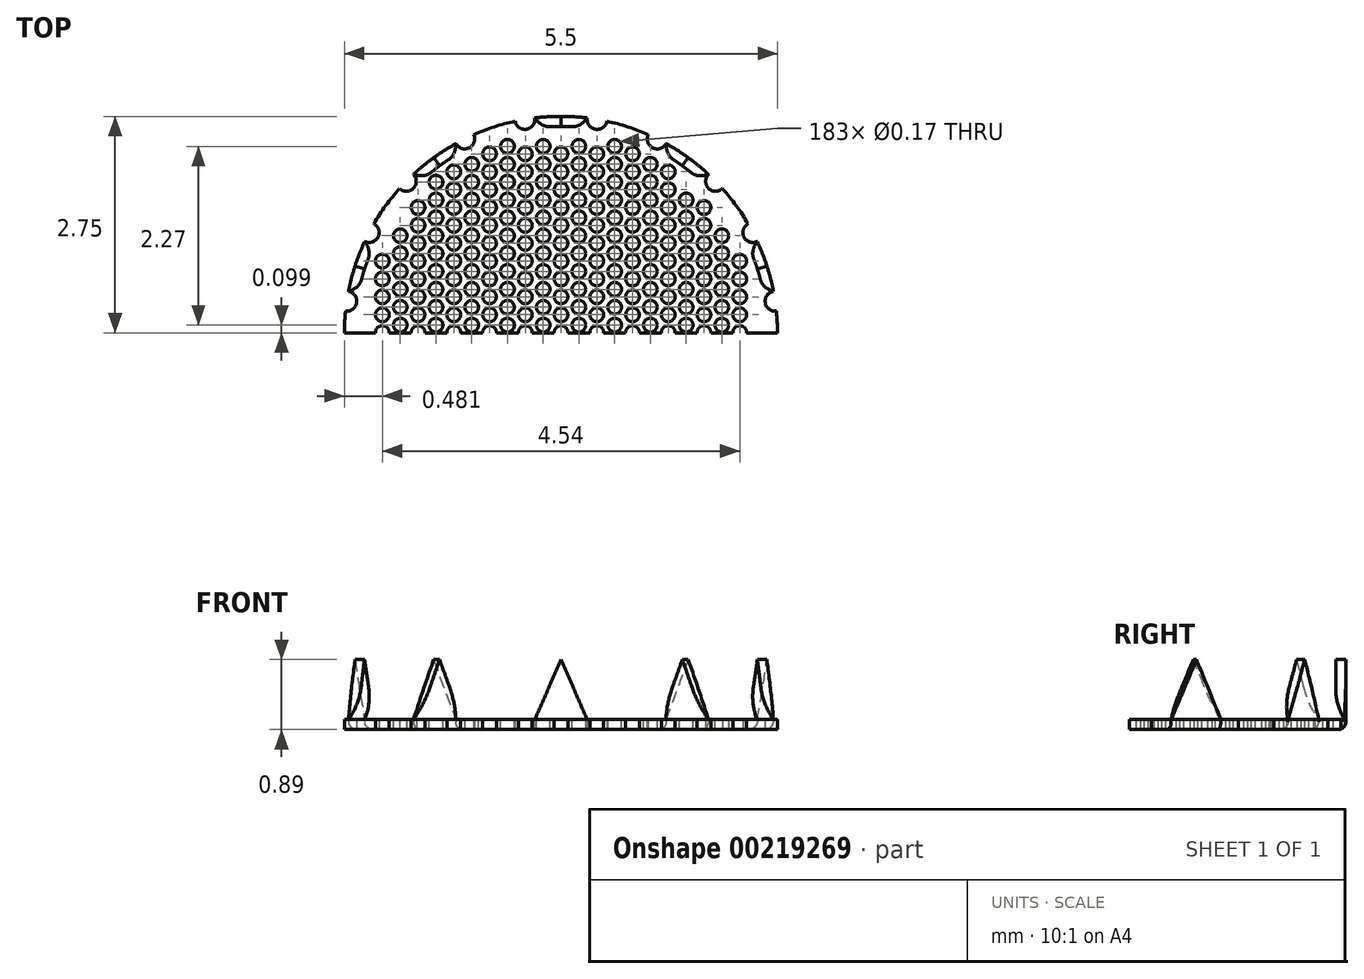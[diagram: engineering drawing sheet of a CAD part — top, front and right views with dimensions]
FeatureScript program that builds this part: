
annotation { "Feature Type Name" : "Feature", "Feature Type Description" : "" }
export const myFeature = defineFeature(function(context is Context, id is Id, definition is map)
    precondition{}
    {
        {
            var Q0;
            Q0=qCreatedBy(makeId("Top.planeOp"),FACE);
            var sketch = newSketch(context, id + "F0", { "sketchPlane" : qUnion([Q0])});
            skCircle(sketch, "E0", {"center": v(0, 0) * mm, "radius": 2.5 * mm});
            skArc(sketch, "E1", {"start": v(0.33, 2.73) * mm, "mid": v(0, 2.75) * mm, "end": v(-0.33, 2.73) * mm});
            skPoint(sketch, "E2", {"position": v(0, 2.75) * mm});
            skLineSegment(sketch, "E3", {"start": v(-3.94, 3.51) * mm, "end": v(3.7, 3.51) * mm, "construction": true});
            skLineSegment(sketch, "E4", {"start": v(0, 3.51) * mm, "end": v(-0.33, 2.73) * mm});
            skLineSegment(sketch, "E5", {"start": v(0, 3.51) * mm, "end": v(0.33, 2.73) * mm});
            skLineSegment(sketch, "E6.1.0", {"start": v(-2.06, 2.84) * mm, "end": v(-1.87, 2.01) * mm});
            skLineSegment(sketch, "E6.1.1", {"start": v(-2.06, 2.84) * mm, "end": v(-1.34, 2.4) * mm});
            skLineSegment(sketch, "E6.2.0", {"start": v(-3.34, 1.09) * mm, "end": v(-2.7, 0.53) * mm});
            skLineSegment(sketch, "E6.2.1", {"start": v(-3.34, 1.09) * mm, "end": v(-2.5, 1.16) * mm});
            skLineSegment(sketch, "E6.3.0", {"start": v(-3.34, -1.09) * mm, "end": v(-2.5, -1.16) * mm});
            skLineSegment(sketch, "E6.3.1", {"start": v(-3.34, -1.09) * mm, "end": v(-2.7, -0.53) * mm});
            skLineSegment(sketch, "E6.4.0", {"start": v(-2.06, -2.84) * mm, "end": v(-1.34, -2.4) * mm});
            skLineSegment(sketch, "E6.4.1", {"start": v(-2.06, -2.84) * mm, "end": v(-1.87, -2.01) * mm});
            skLineSegment(sketch, "E6.5.0", {"start": v(0, -3.51) * mm, "end": v(0.33, -2.73) * mm});
            skLineSegment(sketch, "E6.5.1", {"start": v(0, -3.51) * mm, "end": v(-0.33, -2.73) * mm});
            skLineSegment(sketch, "E6.6.0", {"start": v(2.06, -2.84) * mm, "end": v(1.87, -2.01) * mm});
            skLineSegment(sketch, "E6.6.1", {"start": v(2.06, -2.84) * mm, "end": v(1.34, -2.4) * mm});
            skLineSegment(sketch, "E6.7.0", {"start": v(3.34, -1.09) * mm, "end": v(2.7, -0.53) * mm});
            skLineSegment(sketch, "E6.7.1", {"start": v(3.34, -1.09) * mm, "end": v(2.5, -1.16) * mm});
            skLineSegment(sketch, "E6.8.0", {"start": v(3.34, 1.09) * mm, "end": v(2.5, 1.16) * mm});
            skLineSegment(sketch, "E6.8.1", {"start": v(3.34, 1.09) * mm, "end": v(2.7, 0.53) * mm});
            skLineSegment(sketch, "E6.9.0", {"start": v(2.06, 2.84) * mm, "end": v(1.34, 2.4) * mm});
            skLineSegment(sketch, "E6.9.1", {"start": v(2.06, 2.84) * mm, "end": v(1.87, 2.01) * mm});
            skCircle(sketch, "E7", {"center": v(0, 0) * mm, "radius": 2.62 * mm});
            skPoint(sketch, "E8", {"position": v(0.46, 2.71) * mm});
            skArc(sketch, "E9", {"start": v(0.33, 2.73) * mm, "mid": v(0.44, 2.59) * mm, "end": v(0.58, 2.69) * mm});
            skArc(sketch, "E10.1.0", {"start": v(-1.34, 2.4) * mm, "mid": v(-1.17, 2.35) * mm, "end": v(-1.1, 2.52) * mm});
            skArc(sketch, "E10.2.0", {"start": v(-2.5, 1.16) * mm, "mid": v(-2.32, 1.21) * mm, "end": v(-2.38, 1.38) * mm});
            skArc(sketch, "E10.3.0", {"start": v(-2.7, -0.53) * mm, "mid": v(-2.6, -0.38) * mm, "end": v(-2.74, -0.28) * mm});
            skArc(sketch, "E10.4.0", {"start": v(-1.87, -2.01) * mm, "mid": v(-1.87, -1.84) * mm, "end": v(-2.05, -1.83) * mm});
            skArc(sketch, "E10.5.0", {"start": v(-0.33, -2.73) * mm, "mid": v(-0.44, -2.59) * mm, "end": v(-0.58, -2.69) * mm});
            skArc(sketch, "E10.6.0", {"start": v(1.34, -2.4) * mm, "mid": v(1.17, -2.35) * mm, "end": v(1.1, -2.52) * mm});
            skArc(sketch, "E10.7.0", {"start": v(2.5, -1.16) * mm, "mid": v(2.32, -1.21) * mm, "end": v(2.38, -1.38) * mm});
            skArc(sketch, "E10.8.0", {"start": v(2.7, 0.53) * mm, "mid": v(2.6, 0.38) * mm, "end": v(2.74, 0.28) * mm});
            skArc(sketch, "E10.9.0", {"start": v(1.87, 2.01) * mm, "mid": v(1.87, 1.84) * mm, "end": v(2.05, 1.83) * mm});
            skArc(sketch, "E11", {"start": v(-0.58, 2.69) * mm, "mid": v(-0.44, 2.59) * mm, "end": v(-0.33, 2.73) * mm});
            skArc(sketch, "E12.trimOffspring", {"start": v(-0.58, 2.69) * mm, "mid": v(-0.85, 2.62) * mm, "end": v(-1.1, 2.52) * mm});
            skArc(sketch, "E13.1.0", {"start": v(-2.05, 1.83) * mm, "mid": v(-1.87, 1.84) * mm, "end": v(-1.87, 2.01) * mm});
            skArc(sketch, "E13.2.0", {"start": v(-2.74, 0.28) * mm, "mid": v(-2.6, 0.38) * mm, "end": v(-2.7, 0.53) * mm});
            skArc(sketch, "E13.3.0", {"start": v(-2.38, -1.38) * mm, "mid": v(-2.32, -1.21) * mm, "end": v(-2.5, -1.16) * mm});
            skArc(sketch, "E13.4.0", {"start": v(-1.1, -2.52) * mm, "mid": v(-1.17, -2.35) * mm, "end": v(-1.34, -2.4) * mm});
            skArc(sketch, "E13.5.0", {"start": v(0.58, -2.69) * mm, "mid": v(0.44, -2.59) * mm, "end": v(0.33, -2.73) * mm});
            skArc(sketch, "E13.6.0", {"start": v(2.05, -1.83) * mm, "mid": v(1.87, -1.84) * mm, "end": v(1.87, -2.01) * mm});
            skArc(sketch, "E13.7.0", {"start": v(2.74, -0.28) * mm, "mid": v(2.6, -0.38) * mm, "end": v(2.7, -0.53) * mm});
            skArc(sketch, "E13.8.0", {"start": v(2.38, 1.38) * mm, "mid": v(2.32, 1.21) * mm, "end": v(2.5, 1.16) * mm});
            skArc(sketch, "E13.9.0", {"start": v(1.1, 2.52) * mm, "mid": v(1.17, 2.35) * mm, "end": v(1.34, 2.4) * mm});
            skArc(sketch, "E14.trimOffspring", {"start": v(1.1, 2.52) * mm, "mid": v(0.85, 2.62) * mm, "end": v(0.58, 2.69) * mm});
            skArc(sketch, "E15.trimOffspring", {"start": v(1.87, 2.01) * mm, "mid": v(1.62, 2.22) * mm, "end": v(1.34, 2.4) * mm});
            skArc(sketch, "E16.trimOffspring", {"start": v(2.38, 1.38) * mm, "mid": v(2.22, 1.62) * mm, "end": v(2.05, 1.83) * mm});
            skArc(sketch, "E17.trimOffspring", {"start": v(2.7, 0.53) * mm, "mid": v(2.62, 0.85) * mm, "end": v(2.5, 1.16) * mm});
            skArc(sketch, "E18.trimOffspring", {"start": v(2.74, -0.28) * mm, "mid": v(2.75, 0) * mm, "end": v(2.74, 0.28) * mm});
            skArc(sketch, "E19.trimOffspring", {"start": v(2.5, -1.16) * mm, "mid": v(2.62, -0.85) * mm, "end": v(2.7, -0.53) * mm});
            skArc(sketch, "E20.trimOffspring", {"start": v(2.05, -1.83) * mm, "mid": v(2.22, -1.62) * mm, "end": v(2.38, -1.38) * mm});
            skArc(sketch, "E21.trimOffspring", {"start": v(1.34, -2.4) * mm, "mid": v(1.62, -2.22) * mm, "end": v(1.87, -2.01) * mm});
            skArc(sketch, "E22.trimOffspring", {"start": v(-2.38, -1.38) * mm, "mid": v(-2.22, -1.62) * mm, "end": v(-2.05, -1.83) * mm});
            skArc(sketch, "E23.trimOffspring", {"start": v(-1.87, -2.01) * mm, "mid": v(-1.62, -2.22) * mm, "end": v(-1.34, -2.4) * mm});
            skArc(sketch, "E24.trimOffspring", {"start": v(-1.1, -2.52) * mm, "mid": v(-0.85, -2.62) * mm, "end": v(-0.58, -2.69) * mm});
            skArc(sketch, "E25.trimOffspring", {"start": v(-0.33, -2.73) * mm, "mid": v(0, -2.75) * mm, "end": v(0.33, -2.73) * mm});
            skArc(sketch, "E26.trimOffspring", {"start": v(0.58, -2.69) * mm, "mid": v(0.85, -2.62) * mm, "end": v(1.1, -2.52) * mm});
            skArc(sketch, "E27.trimOffspring", {"start": v(-2.7, -0.53) * mm, "mid": v(-2.62, -0.85) * mm, "end": v(-2.5, -1.16) * mm});
            skArc(sketch, "E28.trimOffspring", {"start": v(-2.74, 0.28) * mm, "mid": v(-2.75, 0) * mm, "end": v(-2.74, -0.28) * mm});
            skArc(sketch, "E29.trimOffspring", {"start": v(-2.5, 1.16) * mm, "mid": v(-2.62, 0.85) * mm, "end": v(-2.7, 0.53) * mm});
            skArc(sketch, "E30.trimOffspring", {"start": v(-2.05, 1.83) * mm, "mid": v(-2.22, 1.62) * mm, "end": v(-2.38, 1.38) * mm});
            skArc(sketch, "E31.trimOffspring", {"start": v(-1.34, 2.4) * mm, "mid": v(-1.62, 2.22) * mm, "end": v(-1.87, 2.01) * mm});
            skSolve(sketch);
        }
        {
            var Q0;
            Q0=qSketchRegion(id+"F0",true);
            var Q1;
            Q1=makeQuery(id+"F0.imprint","IMPRINT",FACE,{"disambiguationData":[TD([[makeQuery(id+"F0.imprint","IMPRINT",EDGE,{"derivedFrom":sQuery(id+"F0.wireOp",EDGE,"E0")}),1.0]])]});
            extrude(context, id + "F1", {"entities" : qUnion([Q0, Q1]), "depth" : 0.13 * mm});
        }
        {
            var Q0;
            Q0=makeQuery(id+"F1.opExtrude","CAP_FACE",FACE,{"disambiguationData":[OSD([sQuery(id+"F0.wireOp",EDGE,"E1"),sQuery(id+"F0.wireOp",EDGE,"E4"),sQuery(id+"F0.wireOp",EDGE,"E5"),sQuery(id+"F0.wireOp",EDGE,"E6.1.0"),sQuery(id+"F0.wireOp",EDGE,"E6.1.1"),sQuery(id+"F0.wireOp",EDGE,"E6.2.0"),sQuery(id+"F0.wireOp",EDGE,"E6.2.1"),sQuery(id+"F0.wireOp",EDGE,"E6.3.0"),sQuery(id+"F0.wireOp",EDGE,"E6.3.1"),sQuery(id+"F0.wireOp",EDGE,"E6.4.0"),sQuery(id+"F0.wireOp",EDGE,"E6.4.1"),sQuery(id+"F0.wireOp",EDGE,"E6.5.0"),sQuery(id+"F0.wireOp",EDGE,"E6.5.1"),sQuery(id+"F0.wireOp",EDGE,"E6.6.0"),sQuery(id+"F0.wireOp",EDGE,"E6.6.1"),sQuery(id+"F0.wireOp",EDGE,"E6.7.0"),sQuery(id+"F0.wireOp",EDGE,"E6.7.1"),sQuery(id+"F0.wireOp",EDGE,"E6.8.0"),sQuery(id+"F0.wireOp",EDGE,"E6.8.1"),sQuery(id+"F0.wireOp",EDGE,"E6.9.0"),sQuery(id+"F0.wireOp",EDGE,"E6.9.1")])],"isStart":false});
            cPlane(context, id + "F2", {"entities" : qUnion([Q0]), "cplaneType" : CPlaneType.OFFSET, "offset" : 0 * mm, "width" : 150 * mm, "height" : 150 * mm});
        }
        {
            var Q0;
            Q0=qCreatedBy(id+"F2.planeOp",FACE);
            var sketch = newSketch(context, id + "F3", { "sketchPlane" : qUnion([Q0])});
            skCircle(sketch, "E32.2.1.8", {"center": v(-2.04, 1.23) * mm, "radius": 0.09 * mm});
            skCircle(sketch, "E32.2.1.9", {"center": v(-2.04, 1) * mm, "radius": 0.09 * mm});
            skCircle(sketch, "E32.0.1.10", {"center": v(-2.27, 0.91) * mm, "radius": 0.09 * mm});
            skCircle(sketch, "E32.2.1.10", {"center": v(-2.04, 0.78) * mm, "radius": 0.09 * mm});
            skCircle(sketch, "E32.2.2.5", {"center": v(-1.59, 1.91) * mm, "radius": 0.09 * mm});
            skCircle(sketch, "E32.2.2.6", {"center": v(-1.59, 1.69) * mm, "radius": 0.09 * mm});
            skCircle(sketch, "E32.0.2.7", {"center": v(-1.82, 1.6) * mm, "radius": 0.09 * mm});
            skCircle(sketch, "E32.2.2.7", {"center": v(-1.59, 1.46) * mm, "radius": 0.09 * mm});
            skCircle(sketch, "E32.0.2.8", {"center": v(-1.82, 1.36) * mm, "radius": 0.09 * mm});
            skCircle(sketch, "E32.2.2.8", {"center": v(-1.59, 1.23) * mm, "radius": 0.09 * mm});
            skCircle(sketch, "E32.0.2.9", {"center": v(-1.82, 1.14) * mm, "radius": 0.09 * mm});
            skCircle(sketch, "E32.2.2.9", {"center": v(-1.59, 1) * mm, "radius": 0.09 * mm});
            skCircle(sketch, "E32.0.2.10", {"center": v(-1.82, 0.91) * mm, "radius": 0.09 * mm});
            skCircle(sketch, "E32.2.2.10", {"center": v(-1.59, 0.78) * mm, "radius": 0.09 * mm});
            skCircle(sketch, "E32.2.3.4", {"center": v(-1.13, 2.14) * mm, "radius": 0.09 * mm});
            skCircle(sketch, "E32.0.3.5", {"center": v(-1.36, 2.05) * mm, "radius": 0.09 * mm});
            skCircle(sketch, "E32.2.3.5", {"center": v(-1.13, 1.91) * mm, "radius": 0.09 * mm});
            skCircle(sketch, "E32.0.3.6", {"center": v(-1.36, 1.82) * mm, "radius": 0.09 * mm});
            skCircle(sketch, "E32.2.3.6", {"center": v(-1.13, 1.69) * mm, "radius": 0.09 * mm});
            skCircle(sketch, "E32.0.3.7", {"center": v(-1.36, 1.6) * mm, "radius": 0.09 * mm});
            skCircle(sketch, "E32.2.3.7", {"center": v(-1.13, 1.46) * mm, "radius": 0.09 * mm});
            skCircle(sketch, "E32.0.3.8", {"center": v(-1.36, 1.36) * mm, "radius": 0.09 * mm});
            skCircle(sketch, "E32.2.3.8", {"center": v(-1.13, 1.23) * mm, "radius": 0.09 * mm});
            skCircle(sketch, "E32.0.3.9", {"center": v(-1.36, 1.14) * mm, "radius": 0.09 * mm});
            skCircle(sketch, "E32.2.3.9", {"center": v(-1.13, 1) * mm, "radius": 0.09 * mm});
            skCircle(sketch, "E32.0.3.10", {"center": v(-1.36, 0.91) * mm, "radius": 0.09 * mm});
            skCircle(sketch, "E32.2.3.10", {"center": v(-1.13, 0.78) * mm, "radius": 0.09 * mm});
            skCircle(sketch, "E32.2.4.3", {"center": v(-0.68, 2.37) * mm, "radius": 0.09 * mm});
            skCircle(sketch, "E32.0.4.4", {"center": v(-0.9, 2.27) * mm, "radius": 0.09 * mm});
            skCircle(sketch, "E32.2.4.4", {"center": v(-0.68, 2.14) * mm, "radius": 0.09 * mm});
            skCircle(sketch, "E32.0.4.5", {"center": v(-0.9, 2.05) * mm, "radius": 0.09 * mm});
            skCircle(sketch, "E32.2.4.5", {"center": v(-0.68, 1.91) * mm, "radius": 0.09 * mm});
            skCircle(sketch, "E32.0.4.6", {"center": v(-0.9, 1.82) * mm, "radius": 0.09 * mm});
            skCircle(sketch, "E32.2.4.6", {"center": v(-0.68, 1.69) * mm, "radius": 0.09 * mm});
            skCircle(sketch, "E32.0.4.7", {"center": v(-0.9, 1.6) * mm, "radius": 0.09 * mm});
            skCircle(sketch, "E32.2.4.7", {"center": v(-0.68, 1.46) * mm, "radius": 0.09 * mm});
            skCircle(sketch, "E32.0.4.8", {"center": v(-0.9, 1.36) * mm, "radius": 0.09 * mm});
            skCircle(sketch, "E32.2.4.8", {"center": v(-0.68, 1.23) * mm, "radius": 0.09 * mm});
            skCircle(sketch, "E32.0.4.9", {"center": v(-0.9, 1.14) * mm, "radius": 0.09 * mm});
            skCircle(sketch, "E32.2.4.9", {"center": v(-0.68, 1) * mm, "radius": 0.09 * mm});
            skCircle(sketch, "E32.0.4.10", {"center": v(-0.9, 0.91) * mm, "radius": 0.09 * mm});
            skCircle(sketch, "E32.2.4.10", {"center": v(-0.68, 0.78) * mm, "radius": 0.09 * mm});
            skCircle(sketch, "E32.2.5.3", {"center": v(-0.23, 2.37) * mm, "radius": 0.09 * mm});
            skCircle(sketch, "E32.0.5.4", {"center": v(-0.45, 2.27) * mm, "radius": 0.09 * mm});
            skCircle(sketch, "E32.2.5.4", {"center": v(-0.23, 2.14) * mm, "radius": 0.09 * mm});
            skCircle(sketch, "E32.0.5.5", {"center": v(-0.45, 2.05) * mm, "radius": 0.09 * mm});
            skCircle(sketch, "E32.2.5.5", {"center": v(-0.23, 1.91) * mm, "radius": 0.09 * mm});
            skCircle(sketch, "E32.0.5.6", {"center": v(-0.45, 1.82) * mm, "radius": 0.09 * mm});
            skCircle(sketch, "E32.2.5.6", {"center": v(-0.23, 1.69) * mm, "radius": 0.09 * mm});
            skCircle(sketch, "E32.0.5.7", {"center": v(-0.45, 1.6) * mm, "radius": 0.09 * mm});
            skCircle(sketch, "E32.2.5.7", {"center": v(-0.23, 1.46) * mm, "radius": 0.09 * mm});
            skCircle(sketch, "E32.0.5.8", {"center": v(-0.45, 1.36) * mm, "radius": 0.09 * mm});
            skCircle(sketch, "E32.2.5.8", {"center": v(-0.23, 1.23) * mm, "radius": 0.09 * mm});
            skCircle(sketch, "E32.0.5.9", {"center": v(-0.45, 1.14) * mm, "radius": 0.09 * mm});
            skCircle(sketch, "E32.2.5.9", {"center": v(-0.23, 1) * mm, "radius": 0.09 * mm});
            skCircle(sketch, "E32.0.5.10", {"center": v(-0.45, 0.91) * mm, "radius": 0.09 * mm});
            skCircle(sketch, "E32.2.5.10", {"center": v(-0.23, 0.78) * mm, "radius": 0.09 * mm});
            skCircle(sketch, "E32.2.6.3", {"center": v(0.23, 2.37) * mm, "radius": 0.09 * mm});
            skCircle(sketch, "E32.0.6.4", {"center": v(0, 2.27) * mm, "radius": 0.09 * mm});
            skCircle(sketch, "E32.2.6.4", {"center": v(0.23, 2.14) * mm, "radius": 0.09 * mm});
            skCircle(sketch, "E32.0.6.5", {"center": v(0, 2.05) * mm, "radius": 0.09 * mm});
            skCircle(sketch, "E32.2.6.5", {"center": v(0.23, 1.91) * mm, "radius": 0.09 * mm});
            skCircle(sketch, "E32.0.6.6", {"center": v(0, 1.82) * mm, "radius": 0.09 * mm});
            skCircle(sketch, "E32.2.6.6", {"center": v(0.23, 1.69) * mm, "radius": 0.09 * mm});
            skCircle(sketch, "E32.0.6.7", {"center": v(0, 1.6) * mm, "radius": 0.09 * mm});
            skCircle(sketch, "E32.2.6.7", {"center": v(0.23, 1.46) * mm, "radius": 0.09 * mm});
            skCircle(sketch, "E32.0.6.8", {"center": v(0, 1.36) * mm, "radius": 0.09 * mm});
            skCircle(sketch, "E32.2.6.8", {"center": v(0.23, 1.23) * mm, "radius": 0.09 * mm});
            skCircle(sketch, "E32.0.6.9", {"center": v(0, 1.14) * mm, "radius": 0.09 * mm});
            skCircle(sketch, "E32.2.6.9", {"center": v(0.23, 1) * mm, "radius": 0.09 * mm});
            skCircle(sketch, "E32.0.6.10", {"center": v(0, 0.91) * mm, "radius": 0.09 * mm});
            skCircle(sketch, "E32.2.6.10", {"center": v(0.23, 0.78) * mm, "radius": 0.09 * mm});
            skCircle(sketch, "E32.2.7.3", {"center": v(0.68, 2.37) * mm, "radius": 0.09 * mm});
            skCircle(sketch, "E32.0.7.4", {"center": v(0.45, 2.27) * mm, "radius": 0.09 * mm});
            skCircle(sketch, "E32.2.7.4", {"center": v(0.68, 2.14) * mm, "radius": 0.09 * mm});
            skCircle(sketch, "E32.0.7.5", {"center": v(0.45, 2.05) * mm, "radius": 0.09 * mm});
            skCircle(sketch, "E32.2.7.5", {"center": v(0.68, 1.91) * mm, "radius": 0.09 * mm});
            skCircle(sketch, "E32.0.7.6", {"center": v(0.45, 1.82) * mm, "radius": 0.09 * mm});
            skCircle(sketch, "E32.2.7.6", {"center": v(0.68, 1.69) * mm, "radius": 0.09 * mm});
            skCircle(sketch, "E32.0.7.7", {"center": v(0.45, 1.6) * mm, "radius": 0.09 * mm});
            skCircle(sketch, "E32.2.7.7", {"center": v(0.68, 1.46) * mm, "radius": 0.09 * mm});
            skCircle(sketch, "E32.0.7.8", {"center": v(0.45, 1.36) * mm, "radius": 0.09 * mm});
            skCircle(sketch, "E32.2.7.8", {"center": v(0.68, 1.23) * mm, "radius": 0.09 * mm});
            skCircle(sketch, "E32.0.7.9", {"center": v(0.45, 1.14) * mm, "radius": 0.09 * mm});
            skCircle(sketch, "E32.2.7.9", {"center": v(0.68, 1) * mm, "radius": 0.09 * mm});
            skCircle(sketch, "E32.0.7.10", {"center": v(0.45, 0.91) * mm, "radius": 0.09 * mm});
            skCircle(sketch, "E32.2.7.10", {"center": v(0.68, 0.78) * mm, "radius": 0.09 * mm});
            skCircle(sketch, "E32.0.8.4", {"center": v(0.9, 2.27) * mm, "radius": 0.09 * mm});
            skCircle(sketch, "E32.2.8.4", {"center": v(1.14, 2.14) * mm, "radius": 0.09 * mm});
            skCircle(sketch, "E32.0.8.5", {"center": v(0.9, 2.05) * mm, "radius": 0.09 * mm});
            skCircle(sketch, "E32.2.8.5", {"center": v(1.14, 1.91) * mm, "radius": 0.09 * mm});
            skCircle(sketch, "E32.0.8.6", {"center": v(0.9, 1.82) * mm, "radius": 0.09 * mm});
            skCircle(sketch, "E32.2.8.6", {"center": v(1.14, 1.69) * mm, "radius": 0.09 * mm});
            skCircle(sketch, "E32.0.8.7", {"center": v(0.9, 1.6) * mm, "radius": 0.09 * mm});
            skCircle(sketch, "E32.2.8.7", {"center": v(1.14, 1.46) * mm, "radius": 0.09 * mm});
            skCircle(sketch, "E32.0.8.8", {"center": v(0.9, 1.36) * mm, "radius": 0.09 * mm});
            skCircle(sketch, "E32.2.8.8", {"center": v(1.14, 1.23) * mm, "radius": 0.09 * mm});
            skCircle(sketch, "E32.0.8.9", {"center": v(0.9, 1.14) * mm, "radius": 0.09 * mm});
            skCircle(sketch, "E32.2.8.9", {"center": v(1.14, 1) * mm, "radius": 0.09 * mm});
            skCircle(sketch, "E32.0.8.10", {"center": v(0.9, 0.91) * mm, "radius": 0.09 * mm});
            skCircle(sketch, "E32.2.8.10", {"center": v(1.14, 0.78) * mm, "radius": 0.09 * mm});
            skCircle(sketch, "E32.0.9.5", {"center": v(1.36, 2.05) * mm, "radius": 0.09 * mm});
            skCircle(sketch, "E32.0.9.6", {"center": v(1.36, 1.82) * mm, "radius": 0.09 * mm});
            skCircle(sketch, "E32.2.9.6", {"center": v(1.6, 1.69) * mm, "radius": 0.09 * mm});
            skCircle(sketch, "E32.0.9.7", {"center": v(1.36, 1.6) * mm, "radius": 0.09 * mm});
            skCircle(sketch, "E32.2.9.7", {"center": v(1.6, 1.46) * mm, "radius": 0.09 * mm});
            skCircle(sketch, "E32.0.9.8", {"center": v(1.36, 1.36) * mm, "radius": 0.09 * mm});
            skCircle(sketch, "E32.2.9.8", {"center": v(1.6, 1.23) * mm, "radius": 0.09 * mm});
            skCircle(sketch, "E32.0.9.9", {"center": v(1.36, 1.14) * mm, "radius": 0.09 * mm});
            skCircle(sketch, "E32.2.9.9", {"center": v(1.6, 1) * mm, "radius": 0.09 * mm});
            skCircle(sketch, "E32.0.9.10", {"center": v(1.36, 0.91) * mm, "radius": 0.09 * mm});
            skCircle(sketch, "E32.2.9.10", {"center": v(1.6, 0.78) * mm, "radius": 0.09 * mm});
            skCircle(sketch, "E32.0.10.7", {"center": v(1.82, 1.6) * mm, "radius": 0.09 * mm});
            skCircle(sketch, "E32.0.10.8", {"center": v(1.82, 1.36) * mm, "radius": 0.09 * mm});
            skCircle(sketch, "E32.2.10.8", {"center": v(2.04, 1.23) * mm, "radius": 0.09 * mm});
            skCircle(sketch, "E32.0.10.9", {"center": v(1.82, 1.14) * mm, "radius": 0.09 * mm});
            skCircle(sketch, "E32.2.10.9", {"center": v(2.04, 1) * mm, "radius": 0.09 * mm});
            skCircle(sketch, "E32.0.10.10", {"center": v(1.82, 0.91) * mm, "radius": 0.09 * mm});
            skCircle(sketch, "E32.2.10.10", {"center": v(2.04, 0.78) * mm, "radius": 0.09 * mm});
            skCircle(sketch, "E33.0.1.11", {"center": v(-2.27, 0.68) * mm, "radius": 0.09 * mm});
            skCircle(sketch, "E33.2.1.11", {"center": v(-2.04, 0.55) * mm, "radius": 0.09 * mm});
            skCircle(sketch, "E33.0.1.12", {"center": v(-2.27, 0.46) * mm, "radius": 0.09 * mm});
            skCircle(sketch, "E33.2.1.12", {"center": v(-2.04, 0.33) * mm, "radius": 0.09 * mm});
            skCircle(sketch, "E33.0.1.13", {"center": v(-2.27, 0.23) * mm, "radius": 0.09 * mm});
            skCircle(sketch, "E33.2.1.13", {"center": v(-2.04, 0.1) * mm, "radius": 0.09 * mm});
            skCircle(sketch, "E33.0.1.14", {"center": v(-2.27, 0) * mm, "radius": 0.09 * mm});
            skCircle(sketch, "E33.2.1.14", {"center": v(-2.04, -0.13) * mm, "radius": 0.09 * mm});
            skCircle(sketch, "E33.0.1.15", {"center": v(-2.27, -0.22) * mm, "radius": 0.09 * mm});
            skCircle(sketch, "E33.2.1.15", {"center": v(-2.04, -0.36) * mm, "radius": 0.09 * mm});
            skCircle(sketch, "E33.0.1.16", {"center": v(-2.27, -0.45) * mm, "radius": 0.09 * mm});
            skCircle(sketch, "E33.2.1.16", {"center": v(-2.04, -0.58) * mm, "radius": 0.09 * mm});
            skCircle(sketch, "E33.0.1.17", {"center": v(-2.27, -0.68) * mm, "radius": 0.09 * mm});
            skCircle(sketch, "E33.2.1.17", {"center": v(-2.04, -0.8) * mm, "radius": 0.09 * mm});
            skCircle(sketch, "E33.0.1.18", {"center": v(-2.27, -0.9) * mm, "radius": 0.09 * mm});
            skCircle(sketch, "E33.2.1.18", {"center": v(-2.04, -1.04) * mm, "radius": 0.09 * mm});
            skCircle(sketch, "E33.2.1.19", {"center": v(-2.04, -1.26) * mm, "radius": 0.09 * mm});
            skCircle(sketch, "E33.0.2.11", {"center": v(-1.82, 0.68) * mm, "radius": 0.09 * mm});
            skCircle(sketch, "E33.2.2.11", {"center": v(-1.59, 0.55) * mm, "radius": 0.09 * mm});
            skCircle(sketch, "E33.0.2.12", {"center": v(-1.82, 0.46) * mm, "radius": 0.09 * mm});
            skCircle(sketch, "E33.2.2.12", {"center": v(-1.59, 0.33) * mm, "radius": 0.09 * mm});
            skCircle(sketch, "E33.0.2.13", {"center": v(-1.82, 0.23) * mm, "radius": 0.09 * mm});
            skCircle(sketch, "E33.2.2.13", {"center": v(-1.59, 0.1) * mm, "radius": 0.09 * mm});
            skCircle(sketch, "E33.0.2.14", {"center": v(-1.82, 0) * mm, "radius": 0.09 * mm});
            skCircle(sketch, "E33.2.2.14", {"center": v(-1.59, -0.13) * mm, "radius": 0.09 * mm});
            skCircle(sketch, "E33.0.2.15", {"center": v(-1.82, -0.22) * mm, "radius": 0.09 * mm});
            skCircle(sketch, "E33.2.2.15", {"center": v(-1.59, -0.36) * mm, "radius": 0.09 * mm});
            skCircle(sketch, "E33.0.2.16", {"center": v(-1.82, -0.45) * mm, "radius": 0.09 * mm});
            skCircle(sketch, "E33.2.2.16", {"center": v(-1.59, -0.58) * mm, "radius": 0.09 * mm});
            skCircle(sketch, "E33.0.2.17", {"center": v(-1.82, -0.68) * mm, "radius": 0.09 * mm});
            skCircle(sketch, "E33.2.2.17", {"center": v(-1.59, -0.8) * mm, "radius": 0.09 * mm});
            skCircle(sketch, "E33.0.2.18", {"center": v(-1.82, -0.9) * mm, "radius": 0.09 * mm});
            skCircle(sketch, "E33.2.2.18", {"center": v(-1.59, -1.04) * mm, "radius": 0.09 * mm});
            skCircle(sketch, "E33.0.2.19", {"center": v(-1.82, -1.13) * mm, "radius": 0.09 * mm});
            skCircle(sketch, "E33.2.2.19", {"center": v(-1.59, -1.26) * mm, "radius": 0.09 * mm});
            skCircle(sketch, "E33.0.2.20", {"center": v(-1.82, -1.36) * mm, "radius": 0.09 * mm});
            skCircle(sketch, "E33.2.2.20", {"center": v(-1.59, -1.5) * mm, "radius": 0.09 * mm});
            skCircle(sketch, "E33.0.2.21", {"center": v(-1.82, -1.59) * mm, "radius": 0.09 * mm});
            skCircle(sketch, "E33.2.2.21", {"center": v(-1.59, -1.72) * mm, "radius": 0.09 * mm});
            skCircle(sketch, "E33.0.3.11", {"center": v(-1.36, 0.68) * mm, "radius": 0.09 * mm});
            skCircle(sketch, "E33.2.3.11", {"center": v(-1.13, 0.55) * mm, "radius": 0.09 * mm});
            skCircle(sketch, "E33.0.3.12", {"center": v(-1.36, 0.46) * mm, "radius": 0.09 * mm});
            skCircle(sketch, "E33.2.3.12", {"center": v(-1.13, 0.33) * mm, "radius": 0.09 * mm});
            skCircle(sketch, "E33.0.3.13", {"center": v(-1.36, 0.23) * mm, "radius": 0.09 * mm});
            skCircle(sketch, "E33.2.3.13", {"center": v(-1.13, 0.1) * mm, "radius": 0.09 * mm});
            skCircle(sketch, "E33.0.3.14", {"center": v(-1.36, 0) * mm, "radius": 0.09 * mm});
            skCircle(sketch, "E33.2.3.14", {"center": v(-1.13, -0.13) * mm, "radius": 0.09 * mm});
            skCircle(sketch, "E33.0.3.15", {"center": v(-1.36, -0.22) * mm, "radius": 0.09 * mm});
            skCircle(sketch, "E33.2.3.15", {"center": v(-1.13, -0.36) * mm, "radius": 0.09 * mm});
            skCircle(sketch, "E33.0.3.16", {"center": v(-1.36, -0.45) * mm, "radius": 0.09 * mm});
            skCircle(sketch, "E33.2.3.16", {"center": v(-1.13, -0.58) * mm, "radius": 0.09 * mm});
            skCircle(sketch, "E33.0.3.17", {"center": v(-1.36, -0.68) * mm, "radius": 0.09 * mm});
            skCircle(sketch, "E33.2.3.17", {"center": v(-1.13, -0.8) * mm, "radius": 0.09 * mm});
            skCircle(sketch, "E33.0.3.18", {"center": v(-1.36, -0.9) * mm, "radius": 0.09 * mm});
            skCircle(sketch, "E33.2.3.18", {"center": v(-1.13, -1.04) * mm, "radius": 0.09 * mm});
            skCircle(sketch, "E33.0.3.19", {"center": v(-1.36, -1.13) * mm, "radius": 0.09 * mm});
            skCircle(sketch, "E33.2.3.19", {"center": v(-1.13, -1.26) * mm, "radius": 0.09 * mm});
            skCircle(sketch, "E33.0.3.20", {"center": v(-1.36, -1.36) * mm, "radius": 0.09 * mm});
            skCircle(sketch, "E33.2.3.20", {"center": v(-1.13, -1.5) * mm, "radius": 0.09 * mm});
            skCircle(sketch, "E33.0.3.21", {"center": v(-1.36, -1.59) * mm, "radius": 0.09 * mm});
            skCircle(sketch, "E33.2.3.21", {"center": v(-1.13, -1.72) * mm, "radius": 0.09 * mm});
            skCircle(sketch, "E33.0.4.11", {"center": v(-0.9, 0.68) * mm, "radius": 0.09 * mm});
            skCircle(sketch, "E33.2.4.11", {"center": v(-0.68, 0.55) * mm, "radius": 0.09 * mm});
            skCircle(sketch, "E33.0.4.12", {"center": v(-0.9, 0.46) * mm, "radius": 0.09 * mm});
            skCircle(sketch, "E33.2.4.12", {"center": v(-0.68, 0.33) * mm, "radius": 0.09 * mm});
            skCircle(sketch, "E33.0.4.13", {"center": v(-0.9, 0.23) * mm, "radius": 0.09 * mm});
            skCircle(sketch, "E33.2.4.13", {"center": v(-0.68, 0.1) * mm, "radius": 0.09 * mm});
            skCircle(sketch, "E33.0.4.14", {"center": v(-0.9, 0) * mm, "radius": 0.09 * mm});
            skCircle(sketch, "E33.2.4.14", {"center": v(-0.68, -0.13) * mm, "radius": 0.09 * mm});
            skCircle(sketch, "E33.0.4.15", {"center": v(-0.9, -0.22) * mm, "radius": 0.09 * mm});
            skCircle(sketch, "E33.2.4.15", {"center": v(-0.68, -0.36) * mm, "radius": 0.09 * mm});
            skCircle(sketch, "E33.0.4.16", {"center": v(-0.9, -0.45) * mm, "radius": 0.09 * mm});
            skCircle(sketch, "E33.2.4.16", {"center": v(-0.68, -0.58) * mm, "radius": 0.09 * mm});
            skCircle(sketch, "E33.0.4.17", {"center": v(-0.9, -0.68) * mm, "radius": 0.09 * mm});
            skCircle(sketch, "E33.2.4.17", {"center": v(-0.68, -0.8) * mm, "radius": 0.09 * mm});
            skCircle(sketch, "E33.0.4.18", {"center": v(-0.9, -0.9) * mm, "radius": 0.09 * mm});
            skCircle(sketch, "E33.2.4.18", {"center": v(-0.68, -1.04) * mm, "radius": 0.09 * mm});
            skCircle(sketch, "E33.0.4.19", {"center": v(-0.9, -1.13) * mm, "radius": 0.09 * mm});
            skCircle(sketch, "E33.2.4.19", {"center": v(-0.68, -1.26) * mm, "radius": 0.09 * mm});
            skCircle(sketch, "E33.0.4.20", {"center": v(-0.9, -1.36) * mm, "radius": 0.09 * mm});
            skCircle(sketch, "E33.2.4.20", {"center": v(-0.68, -1.5) * mm, "radius": 0.09 * mm});
            skCircle(sketch, "E33.0.4.21", {"center": v(-0.9, -1.59) * mm, "radius": 0.09 * mm});
            skCircle(sketch, "E33.2.4.21", {"center": v(-0.68, -1.72) * mm, "radius": 0.09 * mm});
            skCircle(sketch, "E33.0.5.11", {"center": v(-0.45, 0.68) * mm, "radius": 0.09 * mm});
            skCircle(sketch, "E33.2.5.11", {"center": v(-0.23, 0.55) * mm, "radius": 0.09 * mm});
            skCircle(sketch, "E33.0.5.12", {"center": v(-0.45, 0.46) * mm, "radius": 0.09 * mm});
            skCircle(sketch, "E33.2.5.12", {"center": v(-0.23, 0.33) * mm, "radius": 0.09 * mm});
            skCircle(sketch, "E33.0.5.13", {"center": v(-0.45, 0.23) * mm, "radius": 0.09 * mm});
            skCircle(sketch, "E33.2.5.13", {"center": v(-0.23, 0.1) * mm, "radius": 0.09 * mm});
            skCircle(sketch, "E33.0.5.14", {"center": v(-0.45, 0) * mm, "radius": 0.09 * mm});
            skCircle(sketch, "E33.2.5.14", {"center": v(-0.23, -0.13) * mm, "radius": 0.09 * mm});
            skCircle(sketch, "E33.0.5.15", {"center": v(-0.45, -0.22) * mm, "radius": 0.09 * mm});
            skCircle(sketch, "E33.2.5.15", {"center": v(-0.23, -0.36) * mm, "radius": 0.09 * mm});
            skCircle(sketch, "E33.0.5.16", {"center": v(-0.45, -0.45) * mm, "radius": 0.09 * mm});
            skCircle(sketch, "E33.2.5.16", {"center": v(-0.23, -0.58) * mm, "radius": 0.09 * mm});
            skCircle(sketch, "E33.0.5.17", {"center": v(-0.45, -0.68) * mm, "radius": 0.09 * mm});
            skCircle(sketch, "E33.2.5.17", {"center": v(-0.23, -0.8) * mm, "radius": 0.09 * mm});
            skCircle(sketch, "E33.0.5.18", {"center": v(-0.45, -0.9) * mm, "radius": 0.09 * mm});
            skCircle(sketch, "E33.2.5.18", {"center": v(-0.23, -1.04) * mm, "radius": 0.09 * mm});
            skCircle(sketch, "E33.0.5.19", {"center": v(-0.45, -1.13) * mm, "radius": 0.09 * mm});
            skCircle(sketch, "E33.2.5.19", {"center": v(-0.23, -1.26) * mm, "radius": 0.09 * mm});
            skCircle(sketch, "E33.0.5.20", {"center": v(-0.45, -1.36) * mm, "radius": 0.09 * mm});
            skCircle(sketch, "E33.2.5.20", {"center": v(-0.23, -1.5) * mm, "radius": 0.09 * mm});
            skCircle(sketch, "E33.0.5.21", {"center": v(-0.45, -1.59) * mm, "radius": 0.09 * mm});
            skCircle(sketch, "E33.2.5.21", {"center": v(-0.23, -1.72) * mm, "radius": 0.09 * mm});
            skCircle(sketch, "E33.0.6.11", {"center": v(0, 0.68) * mm, "radius": 0.09 * mm});
            skCircle(sketch, "E33.2.6.11", {"center": v(0.23, 0.55) * mm, "radius": 0.09 * mm});
            skCircle(sketch, "E33.0.6.12", {"center": v(0, 0.46) * mm, "radius": 0.09 * mm});
            skCircle(sketch, "E33.2.6.12", {"center": v(0.23, 0.33) * mm, "radius": 0.09 * mm});
            skCircle(sketch, "E33.0.6.13", {"center": v(0, 0.23) * mm, "radius": 0.09 * mm});
            skCircle(sketch, "E33.2.6.13", {"center": v(0.23, 0.1) * mm, "radius": 0.09 * mm});
            skCircle(sketch, "E33.0.6.14", {"center": v(0, 0) * mm, "radius": 0.09 * mm});
            skCircle(sketch, "E33.2.6.14", {"center": v(0.23, -0.13) * mm, "radius": 0.09 * mm});
            skCircle(sketch, "E33.0.6.15", {"center": v(0, -0.22) * mm, "radius": 0.09 * mm});
            skCircle(sketch, "E33.2.6.15", {"center": v(0.23, -0.36) * mm, "radius": 0.09 * mm});
            skCircle(sketch, "E33.0.6.16", {"center": v(0, -0.45) * mm, "radius": 0.09 * mm});
            skCircle(sketch, "E33.2.6.16", {"center": v(0.23, -0.58) * mm, "radius": 0.09 * mm});
            skCircle(sketch, "E33.0.6.17", {"center": v(0, -0.68) * mm, "radius": 0.09 * mm});
            skCircle(sketch, "E33.2.6.17", {"center": v(0.23, -0.8) * mm, "radius": 0.09 * mm});
            skCircle(sketch, "E33.0.6.18", {"center": v(0, -0.9) * mm, "radius": 0.09 * mm});
            skCircle(sketch, "E33.2.6.18", {"center": v(0.23, -1.04) * mm, "radius": 0.09 * mm});
            skCircle(sketch, "E33.0.6.19", {"center": v(0, -1.13) * mm, "radius": 0.09 * mm});
            skCircle(sketch, "E33.2.6.19", {"center": v(0.23, -1.26) * mm, "radius": 0.09 * mm});
            skCircle(sketch, "E33.0.6.20", {"center": v(0, -1.36) * mm, "radius": 0.09 * mm});
            skCircle(sketch, "E33.2.6.20", {"center": v(0.23, -1.5) * mm, "radius": 0.09 * mm});
            skCircle(sketch, "E33.0.6.21", {"center": v(0, -1.59) * mm, "radius": 0.09 * mm});
            skCircle(sketch, "E33.2.6.21", {"center": v(0.23, -1.72) * mm, "radius": 0.09 * mm});
            skCircle(sketch, "E33.0.7.11", {"center": v(0.45, 0.68) * mm, "radius": 0.09 * mm});
            skCircle(sketch, "E33.2.7.11", {"center": v(0.68, 0.55) * mm, "radius": 0.09 * mm});
            skCircle(sketch, "E33.0.7.12", {"center": v(0.45, 0.46) * mm, "radius": 0.09 * mm});
            skCircle(sketch, "E33.2.7.12", {"center": v(0.68, 0.33) * mm, "radius": 0.09 * mm});
            skCircle(sketch, "E33.0.7.13", {"center": v(0.45, 0.23) * mm, "radius": 0.09 * mm});
            skCircle(sketch, "E33.2.7.13", {"center": v(0.68, 0.1) * mm, "radius": 0.09 * mm});
            skCircle(sketch, "E33.0.7.14", {"center": v(0.45, 0) * mm, "radius": 0.09 * mm});
            skCircle(sketch, "E33.2.7.14", {"center": v(0.68, -0.13) * mm, "radius": 0.09 * mm});
            skCircle(sketch, "E33.0.7.15", {"center": v(0.45, -0.22) * mm, "radius": 0.09 * mm});
            skCircle(sketch, "E33.2.7.15", {"center": v(0.68, -0.36) * mm, "radius": 0.09 * mm});
            skCircle(sketch, "E33.0.7.16", {"center": v(0.45, -0.45) * mm, "radius": 0.09 * mm});
            skCircle(sketch, "E33.2.7.16", {"center": v(0.68, -0.58) * mm, "radius": 0.09 * mm});
            skCircle(sketch, "E33.0.7.17", {"center": v(0.45, -0.68) * mm, "radius": 0.09 * mm});
            skCircle(sketch, "E33.2.7.17", {"center": v(0.68, -0.8) * mm, "radius": 0.09 * mm});
            skCircle(sketch, "E33.0.7.18", {"center": v(0.45, -0.9) * mm, "radius": 0.09 * mm});
            skCircle(sketch, "E33.2.7.18", {"center": v(0.68, -1.04) * mm, "radius": 0.09 * mm});
            skCircle(sketch, "E33.0.7.19", {"center": v(0.45, -1.13) * mm, "radius": 0.09 * mm});
            skCircle(sketch, "E33.2.7.19", {"center": v(0.68, -1.26) * mm, "radius": 0.09 * mm});
            skCircle(sketch, "E33.0.7.20", {"center": v(0.45, -1.36) * mm, "radius": 0.09 * mm});
            skCircle(sketch, "E33.2.7.20", {"center": v(0.68, -1.5) * mm, "radius": 0.09 * mm});
            skCircle(sketch, "E33.0.7.21", {"center": v(0.45, -1.59) * mm, "radius": 0.09 * mm});
            skCircle(sketch, "E33.2.7.21", {"center": v(0.68, -1.72) * mm, "radius": 0.09 * mm});
            skCircle(sketch, "E33.0.8.11", {"center": v(0.9, 0.68) * mm, "radius": 0.09 * mm});
            skCircle(sketch, "E33.2.8.11", {"center": v(1.14, 0.55) * mm, "radius": 0.09 * mm});
            skCircle(sketch, "E33.0.8.12", {"center": v(0.9, 0.46) * mm, "radius": 0.09 * mm});
            skCircle(sketch, "E33.2.8.12", {"center": v(1.14, 0.33) * mm, "radius": 0.09 * mm});
            skCircle(sketch, "E33.0.8.13", {"center": v(0.9, 0.23) * mm, "radius": 0.09 * mm});
            skCircle(sketch, "E33.2.8.13", {"center": v(1.14, 0.1) * mm, "radius": 0.09 * mm});
            skCircle(sketch, "E33.0.8.14", {"center": v(0.9, 0) * mm, "radius": 0.09 * mm});
            skCircle(sketch, "E33.2.8.14", {"center": v(1.14, -0.13) * mm, "radius": 0.09 * mm});
            skCircle(sketch, "E33.0.8.15", {"center": v(0.9, -0.22) * mm, "radius": 0.09 * mm});
            skCircle(sketch, "E33.2.8.15", {"center": v(1.14, -0.36) * mm, "radius": 0.09 * mm});
            skCircle(sketch, "E33.0.8.16", {"center": v(0.9, -0.45) * mm, "radius": 0.09 * mm});
            skCircle(sketch, "E33.2.8.16", {"center": v(1.14, -0.58) * mm, "radius": 0.09 * mm});
            skCircle(sketch, "E33.0.8.17", {"center": v(0.9, -0.68) * mm, "radius": 0.09 * mm});
            skCircle(sketch, "E33.2.8.17", {"center": v(1.14, -0.8) * mm, "radius": 0.09 * mm});
            skCircle(sketch, "E33.0.8.18", {"center": v(0.9, -0.9) * mm, "radius": 0.09 * mm});
            skCircle(sketch, "E33.2.8.18", {"center": v(1.14, -1.04) * mm, "radius": 0.09 * mm});
            skCircle(sketch, "E33.0.8.19", {"center": v(0.9, -1.13) * mm, "radius": 0.09 * mm});
            skCircle(sketch, "E33.2.8.19", {"center": v(1.14, -1.26) * mm, "radius": 0.09 * mm});
            skCircle(sketch, "E33.0.8.20", {"center": v(0.9, -1.36) * mm, "radius": 0.09 * mm});
            skCircle(sketch, "E33.2.8.20", {"center": v(1.14, -1.5) * mm, "radius": 0.09 * mm});
            skCircle(sketch, "E33.0.8.21", {"center": v(0.9, -1.59) * mm, "radius": 0.09 * mm});
            skCircle(sketch, "E33.2.8.21", {"center": v(1.14, -1.72) * mm, "radius": 0.09 * mm});
            skCircle(sketch, "E33.0.9.11", {"center": v(1.36, 0.68) * mm, "radius": 0.09 * mm});
            skCircle(sketch, "E33.2.9.11", {"center": v(1.6, 0.55) * mm, "radius": 0.09 * mm});
            skCircle(sketch, "E33.0.9.12", {"center": v(1.36, 0.46) * mm, "radius": 0.09 * mm});
            skCircle(sketch, "E33.2.9.12", {"center": v(1.6, 0.33) * mm, "radius": 0.09 * mm});
            skCircle(sketch, "E33.0.9.13", {"center": v(1.36, 0.23) * mm, "radius": 0.09 * mm});
            skCircle(sketch, "E33.2.9.13", {"center": v(1.6, 0.1) * mm, "radius": 0.09 * mm});
            skCircle(sketch, "E33.0.9.14", {"center": v(1.36, 0) * mm, "radius": 0.09 * mm});
            skCircle(sketch, "E33.2.9.14", {"center": v(1.6, -0.13) * mm, "radius": 0.09 * mm});
            skCircle(sketch, "E33.0.9.15", {"center": v(1.36, -0.22) * mm, "radius": 0.09 * mm});
            skCircle(sketch, "E33.2.9.15", {"center": v(1.6, -0.36) * mm, "radius": 0.09 * mm});
            skCircle(sketch, "E33.0.9.16", {"center": v(1.36, -0.45) * mm, "radius": 0.09 * mm});
            skCircle(sketch, "E33.2.9.16", {"center": v(1.6, -0.58) * mm, "radius": 0.09 * mm});
            skCircle(sketch, "E33.0.9.17", {"center": v(1.36, -0.68) * mm, "radius": 0.09 * mm});
            skCircle(sketch, "E33.2.9.17", {"center": v(1.6, -0.8) * mm, "radius": 0.09 * mm});
            skCircle(sketch, "E33.0.9.18", {"center": v(1.36, -0.9) * mm, "radius": 0.09 * mm});
            skCircle(sketch, "E33.2.9.18", {"center": v(1.6, -1.04) * mm, "radius": 0.09 * mm});
            skCircle(sketch, "E33.0.9.19", {"center": v(1.36, -1.13) * mm, "radius": 0.09 * mm});
            skCircle(sketch, "E33.2.9.19", {"center": v(1.6, -1.26) * mm, "radius": 0.09 * mm});
            skCircle(sketch, "E33.0.9.20", {"center": v(1.36, -1.36) * mm, "radius": 0.09 * mm});
            skCircle(sketch, "E33.2.9.20", {"center": v(1.6, -1.5) * mm, "radius": 0.09 * mm});
            skCircle(sketch, "E33.0.9.21", {"center": v(1.36, -1.59) * mm, "radius": 0.09 * mm});
            skCircle(sketch, "E33.2.9.21", {"center": v(1.6, -1.72) * mm, "radius": 0.09 * mm});
            skCircle(sketch, "E33.0.10.11", {"center": v(1.82, 0.68) * mm, "radius": 0.09 * mm});
            skCircle(sketch, "E33.2.10.11", {"center": v(2.04, 0.55) * mm, "radius": 0.09 * mm});
            skCircle(sketch, "E33.0.10.12", {"center": v(1.82, 0.46) * mm, "radius": 0.09 * mm});
            skCircle(sketch, "E33.2.10.12", {"center": v(2.04, 0.33) * mm, "radius": 0.09 * mm});
            skCircle(sketch, "E33.0.10.13", {"center": v(1.82, 0.23) * mm, "radius": 0.09 * mm});
            skCircle(sketch, "E33.2.10.13", {"center": v(2.04, 0.1) * mm, "radius": 0.09 * mm});
            skCircle(sketch, "E33.0.10.14", {"center": v(1.82, 0) * mm, "radius": 0.09 * mm});
            skCircle(sketch, "E33.2.10.14", {"center": v(2.04, -0.13) * mm, "radius": 0.09 * mm});
            skCircle(sketch, "E33.0.10.15", {"center": v(1.82, -0.22) * mm, "radius": 0.09 * mm});
            skCircle(sketch, "E33.2.10.15", {"center": v(2.04, -0.36) * mm, "radius": 0.09 * mm});
            skCircle(sketch, "E33.0.10.16", {"center": v(1.82, -0.45) * mm, "radius": 0.09 * mm});
            skCircle(sketch, "E33.2.10.16", {"center": v(2.04, -0.58) * mm, "radius": 0.09 * mm});
            skCircle(sketch, "E33.0.10.17", {"center": v(1.82, -0.68) * mm, "radius": 0.09 * mm});
            skCircle(sketch, "E33.2.10.17", {"center": v(2.04, -0.8) * mm, "radius": 0.09 * mm});
            skCircle(sketch, "E33.0.10.18", {"center": v(1.82, -0.9) * mm, "radius": 0.09 * mm});
            skCircle(sketch, "E33.2.10.18", {"center": v(2.04, -1.04) * mm, "radius": 0.09 * mm});
            skCircle(sketch, "E33.0.10.19", {"center": v(1.82, -1.13) * mm, "radius": 0.09 * mm});
            skCircle(sketch, "E33.2.10.19", {"center": v(2.04, -1.26) * mm, "radius": 0.09 * mm});
            skCircle(sketch, "E33.0.10.20", {"center": v(1.82, -1.36) * mm, "radius": 0.09 * mm});
            skCircle(sketch, "E33.0.10.21", {"center": v(1.82, -1.59) * mm, "radius": 0.09 * mm});
            skCircle(sketch, "E34.0.11.10", {"center": v(2.27, 0.91) * mm, "radius": 0.09 * mm});
            skCircle(sketch, "E34.0.11.11", {"center": v(2.27, 0.68) * mm, "radius": 0.09 * mm});
            skCircle(sketch, "E34.0.11.12", {"center": v(2.27, 0.46) * mm, "radius": 0.09 * mm});
            skCircle(sketch, "E34.0.11.13", {"center": v(2.27, 0.23) * mm, "radius": 0.09 * mm});
            skCircle(sketch, "E34.0.11.14", {"center": v(2.27, 0) * mm, "radius": 0.09 * mm});
            skCircle(sketch, "E34.0.11.15", {"center": v(2.27, -0.22) * mm, "radius": 0.09 * mm});
            skCircle(sketch, "E34.0.11.16", {"center": v(2.27, -0.45) * mm, "radius": 0.09 * mm});
            skCircle(sketch, "E34.0.11.17", {"center": v(2.27, -0.68) * mm, "radius": 0.09 * mm});
            skCircle(sketch, "E34.0.11.18", {"center": v(2.27, -0.9) * mm, "radius": 0.09 * mm});
            skCircle(sketch, "E35.0.3.22", {"center": v(-1.36, -1.81) * mm, "radius": 0.09 * mm});
            skCircle(sketch, "E35.2.3.22", {"center": v(-1.13, -1.94) * mm, "radius": 0.09 * mm});
            skCircle(sketch, "E35.0.3.23", {"center": v(-1.36, -2.04) * mm, "radius": 0.09 * mm});
            skCircle(sketch, "E35.2.3.23", {"center": v(-1.13, -2.17) * mm, "radius": 0.09 * mm});
            skCircle(sketch, "E35.0.4.22", {"center": v(-0.9, -1.81) * mm, "radius": 0.09 * mm});
            skCircle(sketch, "E35.2.4.22", {"center": v(-0.68, -1.94) * mm, "radius": 0.09 * mm});
            skCircle(sketch, "E35.0.4.23", {"center": v(-0.9, -2.04) * mm, "radius": 0.09 * mm});
            skCircle(sketch, "E35.2.4.23", {"center": v(-0.68, -2.17) * mm, "radius": 0.09 * mm});
            skCircle(sketch, "E35.0.4.24", {"center": v(-0.9, -2.27) * mm, "radius": 0.09 * mm});
            skCircle(sketch, "E35.0.5.22", {"center": v(-0.45, -1.81) * mm, "radius": 0.09 * mm});
            skCircle(sketch, "E35.2.5.22", {"center": v(-0.23, -1.94) * mm, "radius": 0.09 * mm});
            skCircle(sketch, "E35.0.5.23", {"center": v(-0.45, -2.04) * mm, "radius": 0.09 * mm});
            skCircle(sketch, "E35.2.5.23", {"center": v(-0.23, -2.17) * mm, "radius": 0.09 * mm});
            skCircle(sketch, "E35.0.5.24", {"center": v(-0.45, -2.27) * mm, "radius": 0.09 * mm});
            skCircle(sketch, "E35.2.5.24", {"center": v(-0.23, -2.4) * mm, "radius": 0.09 * mm});
            skCircle(sketch, "E35.0.6.22", {"center": v(0, -1.81) * mm, "radius": 0.09 * mm});
            skCircle(sketch, "E35.2.6.22", {"center": v(0.23, -1.94) * mm, "radius": 0.09 * mm});
            skCircle(sketch, "E35.0.6.23", {"center": v(0, -2.04) * mm, "radius": 0.09 * mm});
            skCircle(sketch, "E35.2.6.23", {"center": v(0.23, -2.17) * mm, "radius": 0.09 * mm});
            skCircle(sketch, "E35.0.6.24", {"center": v(0, -2.27) * mm, "radius": 0.09 * mm});
            skCircle(sketch, "E35.2.6.24", {"center": v(0.23, -2.4) * mm, "radius": 0.09 * mm});
            skCircle(sketch, "E35.0.7.22", {"center": v(0.45, -1.81) * mm, "radius": 0.09 * mm});
            skCircle(sketch, "E35.2.7.22", {"center": v(0.68, -1.94) * mm, "radius": 0.09 * mm});
            skCircle(sketch, "E35.0.7.23", {"center": v(0.45, -2.04) * mm, "radius": 0.09 * mm});
            skCircle(sketch, "E35.2.7.23", {"center": v(0.68, -2.17) * mm, "radius": 0.09 * mm});
            skCircle(sketch, "E35.0.7.24", {"center": v(0.45, -2.27) * mm, "radius": 0.09 * mm});
            skCircle(sketch, "E35.0.8.22", {"center": v(0.9, -1.81) * mm, "radius": 0.09 * mm});
            skCircle(sketch, "E35.2.8.22", {"center": v(1.14, -1.94) * mm, "radius": 0.09 * mm});
            skCircle(sketch, "E35.0.8.23", {"center": v(0.9, -2.04) * mm, "radius": 0.09 * mm});
            skCircle(sketch, "E35.2.8.23", {"center": v(1.14, -2.17) * mm, "radius": 0.09 * mm});
            skCircle(sketch, "E35.0.8.24", {"center": v(0.9, -2.27) * mm, "radius": 0.09 * mm});
            skCircle(sketch, "E35.0.9.22", {"center": v(1.36, -1.81) * mm, "radius": 0.09 * mm});
            skCircle(sketch, "E35.0.9.23", {"center": v(1.36, -2.04) * mm, "radius": 0.09 * mm});
            skCircle(sketch, "E36.0", {"center": v(0, 0) * mm, "radius": 2.5 * mm, "construction": true});
            skSolve(sketch);
        }
        {
            var Q0;
            Q0=qSketchRegion(id+"F3",true);
            extrude(context, id + "F4", {"entities" : qUnion([Q0]), "operationType" : NewBodyOperationType.REMOVE, "endBound" : BoundingType.THROUGH_ALL, "oppositeDirection" : true, "depth" : 25 * mm});
        }
        {
            var Q0;
            Q0=makeQuery(id+"F1.opExtrude","CAP_FACE",FACE,{"disambiguationData":[OSD([sQuery(id+"F0.wireOp",EDGE,"E4"),sQuery(id+"F0.wireOp",EDGE,"E5"),sQuery(id+"F0.wireOp",EDGE,"E6.1.0"),sQuery(id+"F0.wireOp",EDGE,"E6.1.1"),sQuery(id+"F0.wireOp",EDGE,"E6.2.0"),sQuery(id+"F0.wireOp",EDGE,"E6.2.1"),sQuery(id+"F0.wireOp",EDGE,"E6.3.0"),sQuery(id+"F0.wireOp",EDGE,"E6.3.1"),sQuery(id+"F0.wireOp",EDGE,"E6.4.0"),sQuery(id+"F0.wireOp",EDGE,"E6.4.1"),sQuery(id+"F0.wireOp",EDGE,"E6.5.0"),sQuery(id+"F0.wireOp",EDGE,"E6.5.1"),sQuery(id+"F0.wireOp",EDGE,"E6.6.0"),sQuery(id+"F0.wireOp",EDGE,"E6.6.1"),sQuery(id+"F0.wireOp",EDGE,"E6.7.0"),sQuery(id+"F0.wireOp",EDGE,"E6.7.1"),sQuery(id+"F0.wireOp",EDGE,"E6.8.0"),sQuery(id+"F0.wireOp",EDGE,"E6.8.1"),sQuery(id+"F0.wireOp",EDGE,"E6.9.0"),sQuery(id+"F0.wireOp",EDGE,"E6.9.1"),sQuery(id+"F0.wireOp",EDGE,"E9"),sQuery(id+"F0.wireOp",EDGE,"E10.1.0"),sQuery(id+"F0.wireOp",EDGE,"E10.2.0"),sQuery(id+"F0.wireOp",EDGE,"E10.3.0"),sQuery(id+"F0.wireOp",EDGE,"E10.4.0"),sQuery(id+"F0.wireOp",EDGE,"E10.5.0"),sQuery(id+"F0.wireOp",EDGE,"E10.6.0"),sQuery(id+"F0.wireOp",EDGE,"E10.7.0"),sQuery(id+"F0.wireOp",EDGE,"E10.8.0"),sQuery(id+"F0.wireOp",EDGE,"E10.9.0"),sQuery(id+"F0.wireOp",EDGE,"E11"),sQuery(id+"F0.wireOp",EDGE,"E12.trimOffspring"),sQuery(id+"F0.wireOp",EDGE,"E13.1.0"),sQuery(id+"F0.wireOp",EDGE,"E13.2.0"),sQuery(id+"F0.wireOp",EDGE,"E13.3.0"),sQuery(id+"F0.wireOp",EDGE,"E13.4.0"),sQuery(id+"F0.wireOp",EDGE,"E13.5.0"),sQuery(id+"F0.wireOp",EDGE,"E13.6.0"),sQuery(id+"F0.wireOp",EDGE,"E13.7.0"),sQuery(id+"F0.wireOp",EDGE,"E13.8.0"),sQuery(id+"F0.wireOp",EDGE,"E13.9.0"),sQuery(id+"F0.wireOp",EDGE,"E14.trimOffspring"),sQuery(id+"F0.wireOp",EDGE,"E16.trimOffspring"),sQuery(id+"F0.wireOp",EDGE,"E18.trimOffspring"),sQuery(id+"F0.wireOp",EDGE,"E20.trimOffspring"),sQuery(id+"F0.wireOp",EDGE,"E22.trimOffspring"),sQuery(id+"F0.wireOp",EDGE,"E24.trimOffspring"),sQuery(id+"F0.wireOp",EDGE,"E26.trimOffspring"),sQuery(id+"F0.wireOp",EDGE,"E28.trimOffspring"),sQuery(id+"F0.wireOp",EDGE,"E30.trimOffspring")])],"isStart":false});
            var sketch = newSketch(context, id + "F5", { "sketchPlane" : qUnion([Q0])});
            skCircle(sketch, "E37", {"center": v(0, 0) * mm, "radius": 2.75 * mm});
            skCircle(sketch, "E38", {"center": v(0, 0) * mm, "radius": 3.85 * mm});
            skSolve(sketch);
        }
        {
            var Q0;
            Q0 = qSketchRegion(id + "F5", true);
            extrude(context, id + "F6", {"entities" : qUnion([Q0]), "operationType" : NewBodyOperationType.REMOVE, "oppositeDirection" : true, "depth" : 25 * mm});
        }
        {
            var Q0;
            Q0=makeQuery(id+"F1.opExtrude","CAP_FACE",FACE,{"disambiguationData":[OSD([sQuery(id+"F0.wireOp",EDGE,"E4"),sQuery(id+"F0.wireOp",EDGE,"E5"),sQuery(id+"F0.wireOp",EDGE,"E6.1.0"),sQuery(id+"F0.wireOp",EDGE,"E6.1.1"),sQuery(id+"F0.wireOp",EDGE,"E6.2.0"),sQuery(id+"F0.wireOp",EDGE,"E6.2.1"),sQuery(id+"F0.wireOp",EDGE,"E6.3.0"),sQuery(id+"F0.wireOp",EDGE,"E6.3.1"),sQuery(id+"F0.wireOp",EDGE,"E6.4.0"),sQuery(id+"F0.wireOp",EDGE,"E6.4.1"),sQuery(id+"F0.wireOp",EDGE,"E6.5.0"),sQuery(id+"F0.wireOp",EDGE,"E6.5.1"),sQuery(id+"F0.wireOp",EDGE,"E6.6.0"),sQuery(id+"F0.wireOp",EDGE,"E6.6.1"),sQuery(id+"F0.wireOp",EDGE,"E6.7.0"),sQuery(id+"F0.wireOp",EDGE,"E6.7.1"),sQuery(id+"F0.wireOp",EDGE,"E6.8.0"),sQuery(id+"F0.wireOp",EDGE,"E6.8.1"),sQuery(id+"F0.wireOp",EDGE,"E6.9.0"),sQuery(id+"F0.wireOp",EDGE,"E6.9.1"),sQuery(id+"F0.wireOp",EDGE,"E9"),sQuery(id+"F0.wireOp",EDGE,"E10.1.0"),sQuery(id+"F0.wireOp",EDGE,"E10.2.0"),sQuery(id+"F0.wireOp",EDGE,"E10.3.0"),sQuery(id+"F0.wireOp",EDGE,"E10.4.0"),sQuery(id+"F0.wireOp",EDGE,"E10.5.0"),sQuery(id+"F0.wireOp",EDGE,"E10.6.0"),sQuery(id+"F0.wireOp",EDGE,"E10.7.0"),sQuery(id+"F0.wireOp",EDGE,"E10.8.0"),sQuery(id+"F0.wireOp",EDGE,"E10.9.0"),sQuery(id+"F0.wireOp",EDGE,"E11"),sQuery(id+"F0.wireOp",EDGE,"E12.trimOffspring"),sQuery(id+"F0.wireOp",EDGE,"E13.1.0"),sQuery(id+"F0.wireOp",EDGE,"E13.2.0"),sQuery(id+"F0.wireOp",EDGE,"E13.3.0"),sQuery(id+"F0.wireOp",EDGE,"E13.4.0"),sQuery(id+"F0.wireOp",EDGE,"E13.5.0"),sQuery(id+"F0.wireOp",EDGE,"E13.6.0"),sQuery(id+"F0.wireOp",EDGE,"E13.7.0"),sQuery(id+"F0.wireOp",EDGE,"E13.8.0"),sQuery(id+"F0.wireOp",EDGE,"E13.9.0"),sQuery(id+"F0.wireOp",EDGE,"E14.trimOffspring"),sQuery(id+"F0.wireOp",EDGE,"E16.trimOffspring"),sQuery(id+"F0.wireOp",EDGE,"E18.trimOffspring"),sQuery(id+"F0.wireOp",EDGE,"E20.trimOffspring"),sQuery(id+"F0.wireOp",EDGE,"E22.trimOffspring"),sQuery(id+"F0.wireOp",EDGE,"E24.trimOffspring"),sQuery(id+"F0.wireOp",EDGE,"E26.trimOffspring"),sQuery(id+"F0.wireOp",EDGE,"E28.trimOffspring"),sQuery(id+"F0.wireOp",EDGE,"E30.trimOffspring")])],"isStart":false});
            var sketch = newSketch(context, id + "F7", { "sketchPlane" : qUnion([Q0])});
            skArc(sketch, "E39.0", {"start": v(-0.58, 2.69) * mm, "mid": v(-0.85, 2.62) * mm, "end": v(-1.1, 2.52) * mm});
            skCircle(sketch, "E40.0", {"center": v(0, 0) * mm, "radius": 2.62 * mm});
            skLineSegment(sketch, "E41", {"start": v(-1.1, 2.52) * mm, "end": v(-1.05, 2.4) * mm});
            skLineSegment(sketch, "E42", {"start": v(-0.58, 2.69) * mm, "end": v(-0.55, 2.57) * mm});
            skLineSegment(sketch, "E43", {"start": v(-0.33, 2.73) * mm, "end": v(-0.31, 2.6) * mm});
            skLineSegment(sketch, "E44", {"start": v(0.33, 2.73) * mm, "end": v(0.31, 2.6) * mm});
            skSolve(sketch);
        }
        {
            var Q0;
            {var subQ0=sQuery(id+"F7.wireOp",EDGE,"E43");Q0=makeQuery(id+"F7.imprint","IMPRINT",FACE,{"disambiguationData":[TD([[makeQuery(id+"F7.imprint","IMPRINT",EDGE,{"derivedFrom":subQ0}),1.0]])]});}
            extrude(context, id + "F8", {"entities" : qUnion([Q0]), "depth" : .762 * mm});
        }
        {
            var Q0;
            Q0=qCreatedBy(makeId("Front.planeOp"),FACE);
            var sketch = newSketch(context, id + "F9", { "sketchPlane" : qUnion([Q0])});
            skLineSegment(sketch, "E45", {"start": v(0, 3.9) * mm, "end": v(0, -4.13) * mm, "construction": true});
            skSolve(sketch);
        }
        {
            var Q0;
            Q0=qCreatedBy(makeId("Front.planeOp"),FACE);
            var sketch = newSketch(context, id + "F10", { "sketchPlane" : qUnion([Q0])});
            skLineSegment(sketch, "E46", {"start": v(0, 0.89) * mm, "end": v(0.33, 0.13) * mm});
            skLineSegment(sketch, "E47", {"start": v(0.33, 0.13) * mm, "end": v(-0.33, 0.13) * mm});
            skLineSegment(sketch, "E48", {"start": v(-0.33, 0.13) * mm, "end": v(0, 0.89) * mm});
            skPoint(sketch, "E49", {"position": v(0, 0.89) * mm});
            skPoint(sketch, "E50", {"position": v(-0.33, 0.13) * mm});
            skPoint(sketch, "E51", {"position": v(0.33, 0.13) * mm});
            skLineSegment(sketch, "E52", {"start": v(0.33, 0.13) * mm, "end": v(0.33, 0.89) * mm});
            skLineSegment(sketch, "E53", {"start": v(0.33, 0.89) * mm, "end": v(-0.33, 0.89) * mm});
            skLineSegment(sketch, "E54", {"start": v(-0.33, 0.89) * mm, "end": v(-0.33, 0.13) * mm});
            skSolve(sketch);
        }
        {
            var Q0;
            {var subQ0=sQuery(id+"F10.wireOp",EDGE,"E46");Q0=makeQuery(id+"F10.imprint","IMPRINT",FACE,{"disambiguationData":[TD([[makeQuery(id+"F10.imprint","IMPRINT",EDGE,{"derivedFrom":subQ0}),1.0]])]});}
            var Q1;
            {var subQ0=sQuery(id+"F10.wireOp",EDGE,"E48");Q1=makeQuery(id+"F10.imprint","IMPRINT",FACE,{"disambiguationData":[TD([[makeQuery(id+"F10.imprint","IMPRINT",EDGE,{"derivedFrom":subQ0}),1.0]])]});}
            extrude(context, id + "F11", {"entities" : qUnion([Q0, Q1]), "operationType" : NewBodyOperationType.REMOVE, "endBound" : BoundingType.THROUGH_ALL, "oppositeDirection" : true, "depth" : 25 * mm});
        }
        {
            var Q0;
            Q0=makeQuery(id+"F8.opExtrude","SWEPT_BODY",BODY,{"disambiguationData":[OSD([sQuery(id+"F5.wireOp",EDGE,"E37"),sQuery(id+"F7.wireOp",EDGE,"E40.0"),sQuery(id+"F7.wireOp",EDGE,"E43"),sQuery(id+"F7.wireOp",EDGE,"E44")])]});
            var Q1;
            Q1=sQuery(id+"F9.wireOp",EDGE,"E45");
            circularPattern(context, id + "F12", {"entities" : qUnion([Q0]), "axis" : qUnion([Q1]), "angle" : 360 * degree, "instanceCount" : 10, "equalSpace" : true});
        }
        {
            var Q0;
            Q0=makeQuery(id+"F6.boolean.opBoolean","INTERSECT",EDGE,{"disambiguationData":[OD(5.0)],"derivedFrom":[makeQuery(id+"F1.opExtrude","CAP_FACE",FACE,{"disambiguationData":[OSD([sQuery(id+"F0.wireOp",EDGE,"E4"),sQuery(id+"F0.wireOp",EDGE,"E5"),sQuery(id+"F0.wireOp",EDGE,"E6.1.0"),sQuery(id+"F0.wireOp",EDGE,"E6.1.1"),sQuery(id+"F0.wireOp",EDGE,"E6.2.0"),sQuery(id+"F0.wireOp",EDGE,"E6.2.1"),sQuery(id+"F0.wireOp",EDGE,"E6.3.0"),sQuery(id+"F0.wireOp",EDGE,"E6.3.1"),sQuery(id+"F0.wireOp",EDGE,"E6.4.0"),sQuery(id+"F0.wireOp",EDGE,"E6.4.1"),sQuery(id+"F0.wireOp",EDGE,"E6.5.0"),sQuery(id+"F0.wireOp",EDGE,"E6.5.1"),sQuery(id+"F0.wireOp",EDGE,"E6.6.0"),sQuery(id+"F0.wireOp",EDGE,"E6.6.1"),sQuery(id+"F0.wireOp",EDGE,"E6.7.0"),sQuery(id+"F0.wireOp",EDGE,"E6.7.1"),sQuery(id+"F0.wireOp",EDGE,"E6.8.0"),sQuery(id+"F0.wireOp",EDGE,"E6.8.1"),sQuery(id+"F0.wireOp",EDGE,"E6.9.0"),sQuery(id+"F0.wireOp",EDGE,"E6.9.1"),sQuery(id+"F0.wireOp",EDGE,"E9"),sQuery(id+"F0.wireOp",EDGE,"E10.1.0"),sQuery(id+"F0.wireOp",EDGE,"E10.2.0"),sQuery(id+"F0.wireOp",EDGE,"E10.3.0"),sQuery(id+"F0.wireOp",EDGE,"E10.4.0"),sQuery(id+"F0.wireOp",EDGE,"E10.5.0"),sQuery(id+"F0.wireOp",EDGE,"E10.6.0"),sQuery(id+"F0.wireOp",EDGE,"E10.7.0"),sQuery(id+"F0.wireOp",EDGE,"E10.8.0"),sQuery(id+"F0.wireOp",EDGE,"E10.9.0"),sQuery(id+"F0.wireOp",EDGE,"E11"),sQuery(id+"F0.wireOp",EDGE,"E12.trimOffspring"),sQuery(id+"F0.wireOp",EDGE,"E13.1.0"),sQuery(id+"F0.wireOp",EDGE,"E13.2.0"),sQuery(id+"F0.wireOp",EDGE,"E13.3.0"),sQuery(id+"F0.wireOp",EDGE,"E13.4.0"),sQuery(id+"F0.wireOp",EDGE,"E13.5.0"),sQuery(id+"F0.wireOp",EDGE,"E13.6.0"),sQuery(id+"F0.wireOp",EDGE,"E13.7.0"),sQuery(id+"F0.wireOp",EDGE,"E13.8.0"),sQuery(id+"F0.wireOp",EDGE,"E13.9.0"),sQuery(id+"F0.wireOp",EDGE,"E14.trimOffspring"),sQuery(id+"F0.wireOp",EDGE,"E16.trimOffspring"),sQuery(id+"F0.wireOp",EDGE,"E18.trimOffspring"),sQuery(id+"F0.wireOp",EDGE,"E20.trimOffspring"),sQuery(id+"F0.wireOp",EDGE,"E22.trimOffspring"),sQuery(id+"F0.wireOp",EDGE,"E24.trimOffspring"),sQuery(id+"F0.wireOp",EDGE,"E26.trimOffspring"),sQuery(id+"F0.wireOp",EDGE,"E28.trimOffspring"),sQuery(id+"F0.wireOp",EDGE,"E30.trimOffspring")])],"isStart":true}),makeQuery(id+"F6.opExtrude","SWEPT_FACE",FACE,{"disambiguationData":[OSD([sQuery(id+"F5.wireOp",EDGE,"E37")])]})]});
            var Q1;
            Q1=makeQuery(id+"F6.boolean.opBoolean","INTERSECT",EDGE,{"disambiguationData":[OD(6.0)],"derivedFrom":[makeQuery(id+"F1.opExtrude","CAP_FACE",FACE,{"disambiguationData":[OSD([sQuery(id+"F0.wireOp",EDGE,"E4"),sQuery(id+"F0.wireOp",EDGE,"E5"),sQuery(id+"F0.wireOp",EDGE,"E6.1.0"),sQuery(id+"F0.wireOp",EDGE,"E6.1.1"),sQuery(id+"F0.wireOp",EDGE,"E6.2.0"),sQuery(id+"F0.wireOp",EDGE,"E6.2.1"),sQuery(id+"F0.wireOp",EDGE,"E6.3.0"),sQuery(id+"F0.wireOp",EDGE,"E6.3.1"),sQuery(id+"F0.wireOp",EDGE,"E6.4.0"),sQuery(id+"F0.wireOp",EDGE,"E6.4.1"),sQuery(id+"F0.wireOp",EDGE,"E6.5.0"),sQuery(id+"F0.wireOp",EDGE,"E6.5.1"),sQuery(id+"F0.wireOp",EDGE,"E6.6.0"),sQuery(id+"F0.wireOp",EDGE,"E6.6.1"),sQuery(id+"F0.wireOp",EDGE,"E6.7.0"),sQuery(id+"F0.wireOp",EDGE,"E6.7.1"),sQuery(id+"F0.wireOp",EDGE,"E6.8.0"),sQuery(id+"F0.wireOp",EDGE,"E6.8.1"),sQuery(id+"F0.wireOp",EDGE,"E6.9.0"),sQuery(id+"F0.wireOp",EDGE,"E6.9.1"),sQuery(id+"F0.wireOp",EDGE,"E9"),sQuery(id+"F0.wireOp",EDGE,"E10.1.0"),sQuery(id+"F0.wireOp",EDGE,"E10.2.0"),sQuery(id+"F0.wireOp",EDGE,"E10.3.0"),sQuery(id+"F0.wireOp",EDGE,"E10.4.0"),sQuery(id+"F0.wireOp",EDGE,"E10.5.0"),sQuery(id+"F0.wireOp",EDGE,"E10.6.0"),sQuery(id+"F0.wireOp",EDGE,"E10.7.0"),sQuery(id+"F0.wireOp",EDGE,"E10.8.0"),sQuery(id+"F0.wireOp",EDGE,"E10.9.0"),sQuery(id+"F0.wireOp",EDGE,"E11"),sQuery(id+"F0.wireOp",EDGE,"E12.trimOffspring"),sQuery(id+"F0.wireOp",EDGE,"E13.1.0"),sQuery(id+"F0.wireOp",EDGE,"E13.2.0"),sQuery(id+"F0.wireOp",EDGE,"E13.3.0"),sQuery(id+"F0.wireOp",EDGE,"E13.4.0"),sQuery(id+"F0.wireOp",EDGE,"E13.5.0"),sQuery(id+"F0.wireOp",EDGE,"E13.6.0"),sQuery(id+"F0.wireOp",EDGE,"E13.7.0"),sQuery(id+"F0.wireOp",EDGE,"E13.8.0"),sQuery(id+"F0.wireOp",EDGE,"E13.9.0"),sQuery(id+"F0.wireOp",EDGE,"E14.trimOffspring"),sQuery(id+"F0.wireOp",EDGE,"E16.trimOffspring"),sQuery(id+"F0.wireOp",EDGE,"E18.trimOffspring"),sQuery(id+"F0.wireOp",EDGE,"E20.trimOffspring"),sQuery(id+"F0.wireOp",EDGE,"E22.trimOffspring"),sQuery(id+"F0.wireOp",EDGE,"E24.trimOffspring"),sQuery(id+"F0.wireOp",EDGE,"E26.trimOffspring"),sQuery(id+"F0.wireOp",EDGE,"E28.trimOffspring"),sQuery(id+"F0.wireOp",EDGE,"E30.trimOffspring")])],"isStart":true}),makeQuery(id+"F6.opExtrude","SWEPT_FACE",FACE,{"disambiguationData":[OSD([sQuery(id+"F5.wireOp",EDGE,"E37")])]})]});
            var Q2;
            Q2=makeQuery(id+"F6.boolean.opBoolean","INTERSECT",EDGE,{"disambiguationData":[OD(7.0)],"derivedFrom":[makeQuery(id+"F1.opExtrude","CAP_FACE",FACE,{"disambiguationData":[OSD([sQuery(id+"F0.wireOp",EDGE,"E4"),sQuery(id+"F0.wireOp",EDGE,"E5"),sQuery(id+"F0.wireOp",EDGE,"E6.1.0"),sQuery(id+"F0.wireOp",EDGE,"E6.1.1"),sQuery(id+"F0.wireOp",EDGE,"E6.2.0"),sQuery(id+"F0.wireOp",EDGE,"E6.2.1"),sQuery(id+"F0.wireOp",EDGE,"E6.3.0"),sQuery(id+"F0.wireOp",EDGE,"E6.3.1"),sQuery(id+"F0.wireOp",EDGE,"E6.4.0"),sQuery(id+"F0.wireOp",EDGE,"E6.4.1"),sQuery(id+"F0.wireOp",EDGE,"E6.5.0"),sQuery(id+"F0.wireOp",EDGE,"E6.5.1"),sQuery(id+"F0.wireOp",EDGE,"E6.6.0"),sQuery(id+"F0.wireOp",EDGE,"E6.6.1"),sQuery(id+"F0.wireOp",EDGE,"E6.7.0"),sQuery(id+"F0.wireOp",EDGE,"E6.7.1"),sQuery(id+"F0.wireOp",EDGE,"E6.8.0"),sQuery(id+"F0.wireOp",EDGE,"E6.8.1"),sQuery(id+"F0.wireOp",EDGE,"E6.9.0"),sQuery(id+"F0.wireOp",EDGE,"E6.9.1"),sQuery(id+"F0.wireOp",EDGE,"E9"),sQuery(id+"F0.wireOp",EDGE,"E10.1.0"),sQuery(id+"F0.wireOp",EDGE,"E10.2.0"),sQuery(id+"F0.wireOp",EDGE,"E10.3.0"),sQuery(id+"F0.wireOp",EDGE,"E10.4.0"),sQuery(id+"F0.wireOp",EDGE,"E10.5.0"),sQuery(id+"F0.wireOp",EDGE,"E10.6.0"),sQuery(id+"F0.wireOp",EDGE,"E10.7.0"),sQuery(id+"F0.wireOp",EDGE,"E10.8.0"),sQuery(id+"F0.wireOp",EDGE,"E10.9.0"),sQuery(id+"F0.wireOp",EDGE,"E11"),sQuery(id+"F0.wireOp",EDGE,"E12.trimOffspring"),sQuery(id+"F0.wireOp",EDGE,"E13.1.0"),sQuery(id+"F0.wireOp",EDGE,"E13.2.0"),sQuery(id+"F0.wireOp",EDGE,"E13.3.0"),sQuery(id+"F0.wireOp",EDGE,"E13.4.0"),sQuery(id+"F0.wireOp",EDGE,"E13.5.0"),sQuery(id+"F0.wireOp",EDGE,"E13.6.0"),sQuery(id+"F0.wireOp",EDGE,"E13.7.0"),sQuery(id+"F0.wireOp",EDGE,"E13.8.0"),sQuery(id+"F0.wireOp",EDGE,"E13.9.0"),sQuery(id+"F0.wireOp",EDGE,"E14.trimOffspring"),sQuery(id+"F0.wireOp",EDGE,"E16.trimOffspring"),sQuery(id+"F0.wireOp",EDGE,"E18.trimOffspring"),sQuery(id+"F0.wireOp",EDGE,"E20.trimOffspring"),sQuery(id+"F0.wireOp",EDGE,"E22.trimOffspring"),sQuery(id+"F0.wireOp",EDGE,"E24.trimOffspring"),sQuery(id+"F0.wireOp",EDGE,"E26.trimOffspring"),sQuery(id+"F0.wireOp",EDGE,"E28.trimOffspring"),sQuery(id+"F0.wireOp",EDGE,"E30.trimOffspring")])],"isStart":true}),makeQuery(id+"F6.opExtrude","SWEPT_FACE",FACE,{"disambiguationData":[OSD([sQuery(id+"F5.wireOp",EDGE,"E37")])]})]});
            var Q3;
            Q3=makeQuery(id+"F6.boolean.opBoolean","INTERSECT",EDGE,{"disambiguationData":[OD(8.0)],"derivedFrom":[makeQuery(id+"F1.opExtrude","CAP_FACE",FACE,{"disambiguationData":[OSD([sQuery(id+"F0.wireOp",EDGE,"E4"),sQuery(id+"F0.wireOp",EDGE,"E5"),sQuery(id+"F0.wireOp",EDGE,"E6.1.0"),sQuery(id+"F0.wireOp",EDGE,"E6.1.1"),sQuery(id+"F0.wireOp",EDGE,"E6.2.0"),sQuery(id+"F0.wireOp",EDGE,"E6.2.1"),sQuery(id+"F0.wireOp",EDGE,"E6.3.0"),sQuery(id+"F0.wireOp",EDGE,"E6.3.1"),sQuery(id+"F0.wireOp",EDGE,"E6.4.0"),sQuery(id+"F0.wireOp",EDGE,"E6.4.1"),sQuery(id+"F0.wireOp",EDGE,"E6.5.0"),sQuery(id+"F0.wireOp",EDGE,"E6.5.1"),sQuery(id+"F0.wireOp",EDGE,"E6.6.0"),sQuery(id+"F0.wireOp",EDGE,"E6.6.1"),sQuery(id+"F0.wireOp",EDGE,"E6.7.0"),sQuery(id+"F0.wireOp",EDGE,"E6.7.1"),sQuery(id+"F0.wireOp",EDGE,"E6.8.0"),sQuery(id+"F0.wireOp",EDGE,"E6.8.1"),sQuery(id+"F0.wireOp",EDGE,"E6.9.0"),sQuery(id+"F0.wireOp",EDGE,"E6.9.1"),sQuery(id+"F0.wireOp",EDGE,"E9"),sQuery(id+"F0.wireOp",EDGE,"E10.1.0"),sQuery(id+"F0.wireOp",EDGE,"E10.2.0"),sQuery(id+"F0.wireOp",EDGE,"E10.3.0"),sQuery(id+"F0.wireOp",EDGE,"E10.4.0"),sQuery(id+"F0.wireOp",EDGE,"E10.5.0"),sQuery(id+"F0.wireOp",EDGE,"E10.6.0"),sQuery(id+"F0.wireOp",EDGE,"E10.7.0"),sQuery(id+"F0.wireOp",EDGE,"E10.8.0"),sQuery(id+"F0.wireOp",EDGE,"E10.9.0"),sQuery(id+"F0.wireOp",EDGE,"E11"),sQuery(id+"F0.wireOp",EDGE,"E12.trimOffspring"),sQuery(id+"F0.wireOp",EDGE,"E13.1.0"),sQuery(id+"F0.wireOp",EDGE,"E13.2.0"),sQuery(id+"F0.wireOp",EDGE,"E13.3.0"),sQuery(id+"F0.wireOp",EDGE,"E13.4.0"),sQuery(id+"F0.wireOp",EDGE,"E13.5.0"),sQuery(id+"F0.wireOp",EDGE,"E13.6.0"),sQuery(id+"F0.wireOp",EDGE,"E13.7.0"),sQuery(id+"F0.wireOp",EDGE,"E13.8.0"),sQuery(id+"F0.wireOp",EDGE,"E13.9.0"),sQuery(id+"F0.wireOp",EDGE,"E14.trimOffspring"),sQuery(id+"F0.wireOp",EDGE,"E16.trimOffspring"),sQuery(id+"F0.wireOp",EDGE,"E18.trimOffspring"),sQuery(id+"F0.wireOp",EDGE,"E20.trimOffspring"),sQuery(id+"F0.wireOp",EDGE,"E22.trimOffspring"),sQuery(id+"F0.wireOp",EDGE,"E24.trimOffspring"),sQuery(id+"F0.wireOp",EDGE,"E26.trimOffspring"),sQuery(id+"F0.wireOp",EDGE,"E28.trimOffspring"),sQuery(id+"F0.wireOp",EDGE,"E30.trimOffspring")])],"isStart":true}),makeQuery(id+"F6.opExtrude","SWEPT_FACE",FACE,{"disambiguationData":[OSD([sQuery(id+"F5.wireOp",EDGE,"E37")])]})]});
            var Q4;
            Q4=makeQuery(id+"F6.boolean.opBoolean","INTERSECT",EDGE,{"disambiguationData":[OD(9.0)],"derivedFrom":[makeQuery(id+"F1.opExtrude","CAP_FACE",FACE,{"disambiguationData":[OSD([sQuery(id+"F0.wireOp",EDGE,"E4"),sQuery(id+"F0.wireOp",EDGE,"E5"),sQuery(id+"F0.wireOp",EDGE,"E6.1.0"),sQuery(id+"F0.wireOp",EDGE,"E6.1.1"),sQuery(id+"F0.wireOp",EDGE,"E6.2.0"),sQuery(id+"F0.wireOp",EDGE,"E6.2.1"),sQuery(id+"F0.wireOp",EDGE,"E6.3.0"),sQuery(id+"F0.wireOp",EDGE,"E6.3.1"),sQuery(id+"F0.wireOp",EDGE,"E6.4.0"),sQuery(id+"F0.wireOp",EDGE,"E6.4.1"),sQuery(id+"F0.wireOp",EDGE,"E6.5.0"),sQuery(id+"F0.wireOp",EDGE,"E6.5.1"),sQuery(id+"F0.wireOp",EDGE,"E6.6.0"),sQuery(id+"F0.wireOp",EDGE,"E6.6.1"),sQuery(id+"F0.wireOp",EDGE,"E6.7.0"),sQuery(id+"F0.wireOp",EDGE,"E6.7.1"),sQuery(id+"F0.wireOp",EDGE,"E6.8.0"),sQuery(id+"F0.wireOp",EDGE,"E6.8.1"),sQuery(id+"F0.wireOp",EDGE,"E6.9.0"),sQuery(id+"F0.wireOp",EDGE,"E6.9.1"),sQuery(id+"F0.wireOp",EDGE,"E9"),sQuery(id+"F0.wireOp",EDGE,"E10.1.0"),sQuery(id+"F0.wireOp",EDGE,"E10.2.0"),sQuery(id+"F0.wireOp",EDGE,"E10.3.0"),sQuery(id+"F0.wireOp",EDGE,"E10.4.0"),sQuery(id+"F0.wireOp",EDGE,"E10.5.0"),sQuery(id+"F0.wireOp",EDGE,"E10.6.0"),sQuery(id+"F0.wireOp",EDGE,"E10.7.0"),sQuery(id+"F0.wireOp",EDGE,"E10.8.0"),sQuery(id+"F0.wireOp",EDGE,"E10.9.0"),sQuery(id+"F0.wireOp",EDGE,"E11"),sQuery(id+"F0.wireOp",EDGE,"E12.trimOffspring"),sQuery(id+"F0.wireOp",EDGE,"E13.1.0"),sQuery(id+"F0.wireOp",EDGE,"E13.2.0"),sQuery(id+"F0.wireOp",EDGE,"E13.3.0"),sQuery(id+"F0.wireOp",EDGE,"E13.4.0"),sQuery(id+"F0.wireOp",EDGE,"E13.5.0"),sQuery(id+"F0.wireOp",EDGE,"E13.6.0"),sQuery(id+"F0.wireOp",EDGE,"E13.7.0"),sQuery(id+"F0.wireOp",EDGE,"E13.8.0"),sQuery(id+"F0.wireOp",EDGE,"E13.9.0"),sQuery(id+"F0.wireOp",EDGE,"E14.trimOffspring"),sQuery(id+"F0.wireOp",EDGE,"E16.trimOffspring"),sQuery(id+"F0.wireOp",EDGE,"E18.trimOffspring"),sQuery(id+"F0.wireOp",EDGE,"E20.trimOffspring"),sQuery(id+"F0.wireOp",EDGE,"E22.trimOffspring"),sQuery(id+"F0.wireOp",EDGE,"E24.trimOffspring"),sQuery(id+"F0.wireOp",EDGE,"E26.trimOffspring"),sQuery(id+"F0.wireOp",EDGE,"E28.trimOffspring"),sQuery(id+"F0.wireOp",EDGE,"E30.trimOffspring")])],"isStart":true}),makeQuery(id+"F6.opExtrude","SWEPT_FACE",FACE,{"disambiguationData":[OSD([sQuery(id+"F5.wireOp",EDGE,"E37")])]})]});
            var Q5;
            Q5=makeQuery(id+"F6.boolean.opBoolean","INTERSECT",EDGE,{"disambiguationData":[OD(0.0)],"derivedFrom":[makeQuery(id+"F1.opExtrude","CAP_FACE",FACE,{"disambiguationData":[OSD([sQuery(id+"F0.wireOp",EDGE,"E4"),sQuery(id+"F0.wireOp",EDGE,"E5"),sQuery(id+"F0.wireOp",EDGE,"E6.1.0"),sQuery(id+"F0.wireOp",EDGE,"E6.1.1"),sQuery(id+"F0.wireOp",EDGE,"E6.2.0"),sQuery(id+"F0.wireOp",EDGE,"E6.2.1"),sQuery(id+"F0.wireOp",EDGE,"E6.3.0"),sQuery(id+"F0.wireOp",EDGE,"E6.3.1"),sQuery(id+"F0.wireOp",EDGE,"E6.4.0"),sQuery(id+"F0.wireOp",EDGE,"E6.4.1"),sQuery(id+"F0.wireOp",EDGE,"E6.5.0"),sQuery(id+"F0.wireOp",EDGE,"E6.5.1"),sQuery(id+"F0.wireOp",EDGE,"E6.6.0"),sQuery(id+"F0.wireOp",EDGE,"E6.6.1"),sQuery(id+"F0.wireOp",EDGE,"E6.7.0"),sQuery(id+"F0.wireOp",EDGE,"E6.7.1"),sQuery(id+"F0.wireOp",EDGE,"E6.8.0"),sQuery(id+"F0.wireOp",EDGE,"E6.8.1"),sQuery(id+"F0.wireOp",EDGE,"E6.9.0"),sQuery(id+"F0.wireOp",EDGE,"E6.9.1"),sQuery(id+"F0.wireOp",EDGE,"E9"),sQuery(id+"F0.wireOp",EDGE,"E10.1.0"),sQuery(id+"F0.wireOp",EDGE,"E10.2.0"),sQuery(id+"F0.wireOp",EDGE,"E10.3.0"),sQuery(id+"F0.wireOp",EDGE,"E10.4.0"),sQuery(id+"F0.wireOp",EDGE,"E10.5.0"),sQuery(id+"F0.wireOp",EDGE,"E10.6.0"),sQuery(id+"F0.wireOp",EDGE,"E10.7.0"),sQuery(id+"F0.wireOp",EDGE,"E10.8.0"),sQuery(id+"F0.wireOp",EDGE,"E10.9.0"),sQuery(id+"F0.wireOp",EDGE,"E11"),sQuery(id+"F0.wireOp",EDGE,"E12.trimOffspring"),sQuery(id+"F0.wireOp",EDGE,"E13.1.0"),sQuery(id+"F0.wireOp",EDGE,"E13.2.0"),sQuery(id+"F0.wireOp",EDGE,"E13.3.0"),sQuery(id+"F0.wireOp",EDGE,"E13.4.0"),sQuery(id+"F0.wireOp",EDGE,"E13.5.0"),sQuery(id+"F0.wireOp",EDGE,"E13.6.0"),sQuery(id+"F0.wireOp",EDGE,"E13.7.0"),sQuery(id+"F0.wireOp",EDGE,"E13.8.0"),sQuery(id+"F0.wireOp",EDGE,"E13.9.0"),sQuery(id+"F0.wireOp",EDGE,"E14.trimOffspring"),sQuery(id+"F0.wireOp",EDGE,"E16.trimOffspring"),sQuery(id+"F0.wireOp",EDGE,"E18.trimOffspring"),sQuery(id+"F0.wireOp",EDGE,"E20.trimOffspring"),sQuery(id+"F0.wireOp",EDGE,"E22.trimOffspring"),sQuery(id+"F0.wireOp",EDGE,"E24.trimOffspring"),sQuery(id+"F0.wireOp",EDGE,"E26.trimOffspring"),sQuery(id+"F0.wireOp",EDGE,"E28.trimOffspring"),sQuery(id+"F0.wireOp",EDGE,"E30.trimOffspring")])],"isStart":true}),makeQuery(id+"F6.opExtrude","SWEPT_FACE",FACE,{"disambiguationData":[OSD([sQuery(id+"F5.wireOp",EDGE,"E37")])]})]});
            var Q6;
            Q6=makeQuery(id+"F6.boolean.opBoolean","INTERSECT",EDGE,{"disambiguationData":[OD(1.0)],"derivedFrom":[makeQuery(id+"F1.opExtrude","CAP_FACE",FACE,{"disambiguationData":[OSD([sQuery(id+"F0.wireOp",EDGE,"E4"),sQuery(id+"F0.wireOp",EDGE,"E5"),sQuery(id+"F0.wireOp",EDGE,"E6.1.0"),sQuery(id+"F0.wireOp",EDGE,"E6.1.1"),sQuery(id+"F0.wireOp",EDGE,"E6.2.0"),sQuery(id+"F0.wireOp",EDGE,"E6.2.1"),sQuery(id+"F0.wireOp",EDGE,"E6.3.0"),sQuery(id+"F0.wireOp",EDGE,"E6.3.1"),sQuery(id+"F0.wireOp",EDGE,"E6.4.0"),sQuery(id+"F0.wireOp",EDGE,"E6.4.1"),sQuery(id+"F0.wireOp",EDGE,"E6.5.0"),sQuery(id+"F0.wireOp",EDGE,"E6.5.1"),sQuery(id+"F0.wireOp",EDGE,"E6.6.0"),sQuery(id+"F0.wireOp",EDGE,"E6.6.1"),sQuery(id+"F0.wireOp",EDGE,"E6.7.0"),sQuery(id+"F0.wireOp",EDGE,"E6.7.1"),sQuery(id+"F0.wireOp",EDGE,"E6.8.0"),sQuery(id+"F0.wireOp",EDGE,"E6.8.1"),sQuery(id+"F0.wireOp",EDGE,"E6.9.0"),sQuery(id+"F0.wireOp",EDGE,"E6.9.1"),sQuery(id+"F0.wireOp",EDGE,"E9"),sQuery(id+"F0.wireOp",EDGE,"E10.1.0"),sQuery(id+"F0.wireOp",EDGE,"E10.2.0"),sQuery(id+"F0.wireOp",EDGE,"E10.3.0"),sQuery(id+"F0.wireOp",EDGE,"E10.4.0"),sQuery(id+"F0.wireOp",EDGE,"E10.5.0"),sQuery(id+"F0.wireOp",EDGE,"E10.6.0"),sQuery(id+"F0.wireOp",EDGE,"E10.7.0"),sQuery(id+"F0.wireOp",EDGE,"E10.8.0"),sQuery(id+"F0.wireOp",EDGE,"E10.9.0"),sQuery(id+"F0.wireOp",EDGE,"E11"),sQuery(id+"F0.wireOp",EDGE,"E12.trimOffspring"),sQuery(id+"F0.wireOp",EDGE,"E13.1.0"),sQuery(id+"F0.wireOp",EDGE,"E13.2.0"),sQuery(id+"F0.wireOp",EDGE,"E13.3.0"),sQuery(id+"F0.wireOp",EDGE,"E13.4.0"),sQuery(id+"F0.wireOp",EDGE,"E13.5.0"),sQuery(id+"F0.wireOp",EDGE,"E13.6.0"),sQuery(id+"F0.wireOp",EDGE,"E13.7.0"),sQuery(id+"F0.wireOp",EDGE,"E13.8.0"),sQuery(id+"F0.wireOp",EDGE,"E13.9.0"),sQuery(id+"F0.wireOp",EDGE,"E14.trimOffspring"),sQuery(id+"F0.wireOp",EDGE,"E16.trimOffspring"),sQuery(id+"F0.wireOp",EDGE,"E18.trimOffspring"),sQuery(id+"F0.wireOp",EDGE,"E20.trimOffspring"),sQuery(id+"F0.wireOp",EDGE,"E22.trimOffspring"),sQuery(id+"F0.wireOp",EDGE,"E24.trimOffspring"),sQuery(id+"F0.wireOp",EDGE,"E26.trimOffspring"),sQuery(id+"F0.wireOp",EDGE,"E28.trimOffspring"),sQuery(id+"F0.wireOp",EDGE,"E30.trimOffspring")])],"isStart":true}),makeQuery(id+"F6.opExtrude","SWEPT_FACE",FACE,{"disambiguationData":[OSD([sQuery(id+"F5.wireOp",EDGE,"E37")])]})]});
            var Q7;
            Q7=makeQuery(id+"F6.boolean.opBoolean","INTERSECT",EDGE,{"disambiguationData":[OD(2.0)],"derivedFrom":[makeQuery(id+"F1.opExtrude","CAP_FACE",FACE,{"disambiguationData":[OSD([sQuery(id+"F0.wireOp",EDGE,"E4"),sQuery(id+"F0.wireOp",EDGE,"E5"),sQuery(id+"F0.wireOp",EDGE,"E6.1.0"),sQuery(id+"F0.wireOp",EDGE,"E6.1.1"),sQuery(id+"F0.wireOp",EDGE,"E6.2.0"),sQuery(id+"F0.wireOp",EDGE,"E6.2.1"),sQuery(id+"F0.wireOp",EDGE,"E6.3.0"),sQuery(id+"F0.wireOp",EDGE,"E6.3.1"),sQuery(id+"F0.wireOp",EDGE,"E6.4.0"),sQuery(id+"F0.wireOp",EDGE,"E6.4.1"),sQuery(id+"F0.wireOp",EDGE,"E6.5.0"),sQuery(id+"F0.wireOp",EDGE,"E6.5.1"),sQuery(id+"F0.wireOp",EDGE,"E6.6.0"),sQuery(id+"F0.wireOp",EDGE,"E6.6.1"),sQuery(id+"F0.wireOp",EDGE,"E6.7.0"),sQuery(id+"F0.wireOp",EDGE,"E6.7.1"),sQuery(id+"F0.wireOp",EDGE,"E6.8.0"),sQuery(id+"F0.wireOp",EDGE,"E6.8.1"),sQuery(id+"F0.wireOp",EDGE,"E6.9.0"),sQuery(id+"F0.wireOp",EDGE,"E6.9.1"),sQuery(id+"F0.wireOp",EDGE,"E9"),sQuery(id+"F0.wireOp",EDGE,"E10.1.0"),sQuery(id+"F0.wireOp",EDGE,"E10.2.0"),sQuery(id+"F0.wireOp",EDGE,"E10.3.0"),sQuery(id+"F0.wireOp",EDGE,"E10.4.0"),sQuery(id+"F0.wireOp",EDGE,"E10.5.0"),sQuery(id+"F0.wireOp",EDGE,"E10.6.0"),sQuery(id+"F0.wireOp",EDGE,"E10.7.0"),sQuery(id+"F0.wireOp",EDGE,"E10.8.0"),sQuery(id+"F0.wireOp",EDGE,"E10.9.0"),sQuery(id+"F0.wireOp",EDGE,"E11"),sQuery(id+"F0.wireOp",EDGE,"E12.trimOffspring"),sQuery(id+"F0.wireOp",EDGE,"E13.1.0"),sQuery(id+"F0.wireOp",EDGE,"E13.2.0"),sQuery(id+"F0.wireOp",EDGE,"E13.3.0"),sQuery(id+"F0.wireOp",EDGE,"E13.4.0"),sQuery(id+"F0.wireOp",EDGE,"E13.5.0"),sQuery(id+"F0.wireOp",EDGE,"E13.6.0"),sQuery(id+"F0.wireOp",EDGE,"E13.7.0"),sQuery(id+"F0.wireOp",EDGE,"E13.8.0"),sQuery(id+"F0.wireOp",EDGE,"E13.9.0"),sQuery(id+"F0.wireOp",EDGE,"E14.trimOffspring"),sQuery(id+"F0.wireOp",EDGE,"E16.trimOffspring"),sQuery(id+"F0.wireOp",EDGE,"E18.trimOffspring"),sQuery(id+"F0.wireOp",EDGE,"E20.trimOffspring"),sQuery(id+"F0.wireOp",EDGE,"E22.trimOffspring"),sQuery(id+"F0.wireOp",EDGE,"E24.trimOffspring"),sQuery(id+"F0.wireOp",EDGE,"E26.trimOffspring"),sQuery(id+"F0.wireOp",EDGE,"E28.trimOffspring"),sQuery(id+"F0.wireOp",EDGE,"E30.trimOffspring")])],"isStart":true}),makeQuery(id+"F6.opExtrude","SWEPT_FACE",FACE,{"disambiguationData":[OSD([sQuery(id+"F5.wireOp",EDGE,"E37")])]})]});
            var Q8;
            Q8=makeQuery(id+"F6.boolean.opBoolean","INTERSECT",EDGE,{"disambiguationData":[OD(3.0)],"derivedFrom":[makeQuery(id+"F1.opExtrude","CAP_FACE",FACE,{"disambiguationData":[OSD([sQuery(id+"F0.wireOp",EDGE,"E4"),sQuery(id+"F0.wireOp",EDGE,"E5"),sQuery(id+"F0.wireOp",EDGE,"E6.1.0"),sQuery(id+"F0.wireOp",EDGE,"E6.1.1"),sQuery(id+"F0.wireOp",EDGE,"E6.2.0"),sQuery(id+"F0.wireOp",EDGE,"E6.2.1"),sQuery(id+"F0.wireOp",EDGE,"E6.3.0"),sQuery(id+"F0.wireOp",EDGE,"E6.3.1"),sQuery(id+"F0.wireOp",EDGE,"E6.4.0"),sQuery(id+"F0.wireOp",EDGE,"E6.4.1"),sQuery(id+"F0.wireOp",EDGE,"E6.5.0"),sQuery(id+"F0.wireOp",EDGE,"E6.5.1"),sQuery(id+"F0.wireOp",EDGE,"E6.6.0"),sQuery(id+"F0.wireOp",EDGE,"E6.6.1"),sQuery(id+"F0.wireOp",EDGE,"E6.7.0"),sQuery(id+"F0.wireOp",EDGE,"E6.7.1"),sQuery(id+"F0.wireOp",EDGE,"E6.8.0"),sQuery(id+"F0.wireOp",EDGE,"E6.8.1"),sQuery(id+"F0.wireOp",EDGE,"E6.9.0"),sQuery(id+"F0.wireOp",EDGE,"E6.9.1"),sQuery(id+"F0.wireOp",EDGE,"E9"),sQuery(id+"F0.wireOp",EDGE,"E10.1.0"),sQuery(id+"F0.wireOp",EDGE,"E10.2.0"),sQuery(id+"F0.wireOp",EDGE,"E10.3.0"),sQuery(id+"F0.wireOp",EDGE,"E10.4.0"),sQuery(id+"F0.wireOp",EDGE,"E10.5.0"),sQuery(id+"F0.wireOp",EDGE,"E10.6.0"),sQuery(id+"F0.wireOp",EDGE,"E10.7.0"),sQuery(id+"F0.wireOp",EDGE,"E10.8.0"),sQuery(id+"F0.wireOp",EDGE,"E10.9.0"),sQuery(id+"F0.wireOp",EDGE,"E11"),sQuery(id+"F0.wireOp",EDGE,"E12.trimOffspring"),sQuery(id+"F0.wireOp",EDGE,"E13.1.0"),sQuery(id+"F0.wireOp",EDGE,"E13.2.0"),sQuery(id+"F0.wireOp",EDGE,"E13.3.0"),sQuery(id+"F0.wireOp",EDGE,"E13.4.0"),sQuery(id+"F0.wireOp",EDGE,"E13.5.0"),sQuery(id+"F0.wireOp",EDGE,"E13.6.0"),sQuery(id+"F0.wireOp",EDGE,"E13.7.0"),sQuery(id+"F0.wireOp",EDGE,"E13.8.0"),sQuery(id+"F0.wireOp",EDGE,"E13.9.0"),sQuery(id+"F0.wireOp",EDGE,"E14.trimOffspring"),sQuery(id+"F0.wireOp",EDGE,"E16.trimOffspring"),sQuery(id+"F0.wireOp",EDGE,"E18.trimOffspring"),sQuery(id+"F0.wireOp",EDGE,"E20.trimOffspring"),sQuery(id+"F0.wireOp",EDGE,"E22.trimOffspring"),sQuery(id+"F0.wireOp",EDGE,"E24.trimOffspring"),sQuery(id+"F0.wireOp",EDGE,"E26.trimOffspring"),sQuery(id+"F0.wireOp",EDGE,"E28.trimOffspring"),sQuery(id+"F0.wireOp",EDGE,"E30.trimOffspring")])],"isStart":true}),makeQuery(id+"F6.opExtrude","SWEPT_FACE",FACE,{"disambiguationData":[OSD([sQuery(id+"F5.wireOp",EDGE,"E37")])]})]});
            var Q9;
            Q9=makeQuery(id+"F6.boolean.opBoolean","INTERSECT",EDGE,{"disambiguationData":[OD(4.0)],"derivedFrom":[makeQuery(id+"F1.opExtrude","CAP_FACE",FACE,{"disambiguationData":[OSD([sQuery(id+"F0.wireOp",EDGE,"E4"),sQuery(id+"F0.wireOp",EDGE,"E5"),sQuery(id+"F0.wireOp",EDGE,"E6.1.0"),sQuery(id+"F0.wireOp",EDGE,"E6.1.1"),sQuery(id+"F0.wireOp",EDGE,"E6.2.0"),sQuery(id+"F0.wireOp",EDGE,"E6.2.1"),sQuery(id+"F0.wireOp",EDGE,"E6.3.0"),sQuery(id+"F0.wireOp",EDGE,"E6.3.1"),sQuery(id+"F0.wireOp",EDGE,"E6.4.0"),sQuery(id+"F0.wireOp",EDGE,"E6.4.1"),sQuery(id+"F0.wireOp",EDGE,"E6.5.0"),sQuery(id+"F0.wireOp",EDGE,"E6.5.1"),sQuery(id+"F0.wireOp",EDGE,"E6.6.0"),sQuery(id+"F0.wireOp",EDGE,"E6.6.1"),sQuery(id+"F0.wireOp",EDGE,"E6.7.0"),sQuery(id+"F0.wireOp",EDGE,"E6.7.1"),sQuery(id+"F0.wireOp",EDGE,"E6.8.0"),sQuery(id+"F0.wireOp",EDGE,"E6.8.1"),sQuery(id+"F0.wireOp",EDGE,"E6.9.0"),sQuery(id+"F0.wireOp",EDGE,"E6.9.1"),sQuery(id+"F0.wireOp",EDGE,"E9"),sQuery(id+"F0.wireOp",EDGE,"E10.1.0"),sQuery(id+"F0.wireOp",EDGE,"E10.2.0"),sQuery(id+"F0.wireOp",EDGE,"E10.3.0"),sQuery(id+"F0.wireOp",EDGE,"E10.4.0"),sQuery(id+"F0.wireOp",EDGE,"E10.5.0"),sQuery(id+"F0.wireOp",EDGE,"E10.6.0"),sQuery(id+"F0.wireOp",EDGE,"E10.7.0"),sQuery(id+"F0.wireOp",EDGE,"E10.8.0"),sQuery(id+"F0.wireOp",EDGE,"E10.9.0"),sQuery(id+"F0.wireOp",EDGE,"E11"),sQuery(id+"F0.wireOp",EDGE,"E12.trimOffspring"),sQuery(id+"F0.wireOp",EDGE,"E13.1.0"),sQuery(id+"F0.wireOp",EDGE,"E13.2.0"),sQuery(id+"F0.wireOp",EDGE,"E13.3.0"),sQuery(id+"F0.wireOp",EDGE,"E13.4.0"),sQuery(id+"F0.wireOp",EDGE,"E13.5.0"),sQuery(id+"F0.wireOp",EDGE,"E13.6.0"),sQuery(id+"F0.wireOp",EDGE,"E13.7.0"),sQuery(id+"F0.wireOp",EDGE,"E13.8.0"),sQuery(id+"F0.wireOp",EDGE,"E13.9.0"),sQuery(id+"F0.wireOp",EDGE,"E14.trimOffspring"),sQuery(id+"F0.wireOp",EDGE,"E16.trimOffspring"),sQuery(id+"F0.wireOp",EDGE,"E18.trimOffspring"),sQuery(id+"F0.wireOp",EDGE,"E20.trimOffspring"),sQuery(id+"F0.wireOp",EDGE,"E22.trimOffspring"),sQuery(id+"F0.wireOp",EDGE,"E24.trimOffspring"),sQuery(id+"F0.wireOp",EDGE,"E26.trimOffspring"),sQuery(id+"F0.wireOp",EDGE,"E28.trimOffspring"),sQuery(id+"F0.wireOp",EDGE,"E30.trimOffspring")])],"isStart":true}),makeQuery(id+"F6.opExtrude","SWEPT_FACE",FACE,{"disambiguationData":[OSD([sQuery(id+"F5.wireOp",EDGE,"E37")])]})]});
            fillet(context, id + "F13", {"entities" : qUnion([Q0, Q1, Q2, Q3, Q4, Q5, Q6, Q7, Q8, Q9]), "radius" : .1 * mm, "tangentPropagation" : true, "allowEdgeOverflow" : false});
        }
        {
            var Q0;
            Q0=makeQuery(id+"F12.opPattern","COPY",EDGE,{"derivedFrom":makeQuery(id+"F8.opExtrude","CAP_EDGE",EDGE,{"disambiguationData":[OSD([sQuery(id+"F7.wireOp",EDGE,"E40.0")])],"isStart":true}),"instanceName":"8"});
            var Q1;
            Q1=makeQuery(id+"F12.opPattern","COPY",EDGE,{"derivedFrom":makeQuery(id+"F8.opExtrude","CAP_EDGE",EDGE,{"disambiguationData":[OSD([sQuery(id+"F7.wireOp",EDGE,"E40.0")])],"isStart":true}),"instanceName":"4"});
            var Q2;
            Q2=makeQuery(id+"F12.opPattern","COPY",EDGE,{"derivedFrom":makeQuery(id+"F8.opExtrude","CAP_EDGE",EDGE,{"disambiguationData":[OSD([sQuery(id+"F7.wireOp",EDGE,"E40.0")])],"isStart":true}),"instanceName":"5"});
            var Q3;
            Q3=makeQuery(id+"F12.opPattern","COPY",EDGE,{"derivedFrom":makeQuery(id+"F8.opExtrude","CAP_EDGE",EDGE,{"disambiguationData":[OSD([sQuery(id+"F7.wireOp",EDGE,"E40.0")])],"isStart":true}),"instanceName":"6"});
            var Q4;
            Q4=makeQuery(id+"F12.opPattern","COPY",EDGE,{"derivedFrom":makeQuery(id+"F8.opExtrude","CAP_EDGE",EDGE,{"disambiguationData":[OSD([sQuery(id+"F7.wireOp",EDGE,"E40.0")])],"isStart":true}),"instanceName":"3"});
            var Q5;
            Q5=makeQuery(id+"F12.opPattern","COPY",EDGE,{"derivedFrom":makeQuery(id+"F8.opExtrude","CAP_EDGE",EDGE,{"disambiguationData":[OSD([sQuery(id+"F7.wireOp",EDGE,"E40.0")])],"isStart":true}),"instanceName":"7"});
            var Q6;
            Q6=makeQuery(id+"F12.opPattern","COPY",EDGE,{"derivedFrom":makeQuery(id+"F8.opExtrude","CAP_EDGE",EDGE,{"disambiguationData":[OSD([sQuery(id+"F7.wireOp",EDGE,"E40.0")])],"isStart":true}),"instanceName":"9"});
            var Q7;
            Q7=makeQuery(id+"F8.opExtrude","CAP_EDGE",EDGE,{"disambiguationData":[OSD([sQuery(id+"F7.wireOp",EDGE,"E40.0")])],"isStart":true});
            var Q8;
            Q8=makeQuery(id+"F12.opPattern","COPY",EDGE,{"derivedFrom":makeQuery(id+"F8.opExtrude","CAP_EDGE",EDGE,{"disambiguationData":[OSD([sQuery(id+"F7.wireOp",EDGE,"E40.0")])],"isStart":true}),"instanceName":"1"});
            var Q9;
            Q9=makeQuery(id+"F12.opPattern","COPY",EDGE,{"derivedFrom":makeQuery(id+"F8.opExtrude","CAP_EDGE",EDGE,{"disambiguationData":[OSD([sQuery(id+"F7.wireOp",EDGE,"E40.0")])],"isStart":true}),"instanceName":"2"});
            fillet(context, id + "F14", {"entities" : qUnion([Q0, Q1, Q2, Q3, Q4, Q5, Q6, Q7, Q8, Q9]), "radius" : .8 * mm, "tangentPropagation" : true, "allowEdgeOverflow" : false});
        }
        {
            var Q0;
            Q0=makeQuery(id+"F1.opExtrude","CAP_FACE",FACE,{"disambiguationData":[OSD([sQuery(id+"F0.wireOp",EDGE,"E4"),sQuery(id+"F0.wireOp",EDGE,"E5"),sQuery(id+"F0.wireOp",EDGE,"E6.1.0"),sQuery(id+"F0.wireOp",EDGE,"E6.1.1"),sQuery(id+"F0.wireOp",EDGE,"E6.2.0"),sQuery(id+"F0.wireOp",EDGE,"E6.2.1"),sQuery(id+"F0.wireOp",EDGE,"E6.3.0"),sQuery(id+"F0.wireOp",EDGE,"E6.3.1"),sQuery(id+"F0.wireOp",EDGE,"E6.4.0"),sQuery(id+"F0.wireOp",EDGE,"E6.4.1"),sQuery(id+"F0.wireOp",EDGE,"E6.5.0"),sQuery(id+"F0.wireOp",EDGE,"E6.5.1"),sQuery(id+"F0.wireOp",EDGE,"E6.6.0"),sQuery(id+"F0.wireOp",EDGE,"E6.6.1"),sQuery(id+"F0.wireOp",EDGE,"E6.7.0"),sQuery(id+"F0.wireOp",EDGE,"E6.7.1"),sQuery(id+"F0.wireOp",EDGE,"E6.8.0"),sQuery(id+"F0.wireOp",EDGE,"E6.8.1"),sQuery(id+"F0.wireOp",EDGE,"E6.9.0"),sQuery(id+"F0.wireOp",EDGE,"E6.9.1"),sQuery(id+"F0.wireOp",EDGE,"E9"),sQuery(id+"F0.wireOp",EDGE,"E10.1.0"),sQuery(id+"F0.wireOp",EDGE,"E10.2.0"),sQuery(id+"F0.wireOp",EDGE,"E10.3.0"),sQuery(id+"F0.wireOp",EDGE,"E10.4.0"),sQuery(id+"F0.wireOp",EDGE,"E10.5.0"),sQuery(id+"F0.wireOp",EDGE,"E10.6.0"),sQuery(id+"F0.wireOp",EDGE,"E10.7.0"),sQuery(id+"F0.wireOp",EDGE,"E10.8.0"),sQuery(id+"F0.wireOp",EDGE,"E10.9.0"),sQuery(id+"F0.wireOp",EDGE,"E11"),sQuery(id+"F0.wireOp",EDGE,"E12.trimOffspring"),sQuery(id+"F0.wireOp",EDGE,"E13.1.0"),sQuery(id+"F0.wireOp",EDGE,"E13.2.0"),sQuery(id+"F0.wireOp",EDGE,"E13.3.0"),sQuery(id+"F0.wireOp",EDGE,"E13.4.0"),sQuery(id+"F0.wireOp",EDGE,"E13.5.0"),sQuery(id+"F0.wireOp",EDGE,"E13.6.0"),sQuery(id+"F0.wireOp",EDGE,"E13.7.0"),sQuery(id+"F0.wireOp",EDGE,"E13.8.0"),sQuery(id+"F0.wireOp",EDGE,"E13.9.0"),sQuery(id+"F0.wireOp",EDGE,"E14.trimOffspring"),sQuery(id+"F0.wireOp",EDGE,"E16.trimOffspring"),sQuery(id+"F0.wireOp",EDGE,"E18.trimOffspring"),sQuery(id+"F0.wireOp",EDGE,"E20.trimOffspring"),sQuery(id+"F0.wireOp",EDGE,"E22.trimOffspring"),sQuery(id+"F0.wireOp",EDGE,"E24.trimOffspring"),sQuery(id+"F0.wireOp",EDGE,"E26.trimOffspring"),sQuery(id+"F0.wireOp",EDGE,"E28.trimOffspring"),sQuery(id+"F0.wireOp",EDGE,"E30.trimOffspring")])],"isStart":false});
            var sketch = newSketch(context, id + "F15", { "sketchPlane" : qUnion([Q0])});
            skLineSegment(sketch, "E55.bottom", {"start": v(-3.26, 0) * mm, "end": v(3.47, 0) * mm});
            skLineSegment(sketch, "E55.top", {"start": v(-3.26, -2.87) * mm, "end": v(3.47, -2.87) * mm});
            skLineSegment(sketch, "E55.left", {"start": v(-3.26, 0) * mm, "end": v(-3.26, -2.87) * mm});
            skLineSegment(sketch, "E55.right", {"start": v(3.47, 0) * mm, "end": v(3.47, -2.87) * mm});
            skSolve(sketch);
        }
        {
            var Q0;
            Q0 = qSketchRegion(id + "F15", true);
            extrude(context, id + "F16", {"entities" : qUnion([Q0]), "operationType" : NewBodyOperationType.REMOVE, "oppositeDirection" : true, "depth" : 25 * mm, "hasSecondDirection" : true, "secondDirectionOppositeDirection" : false, "secondDirectionDepth" : 25 * mm});
        }
    });
